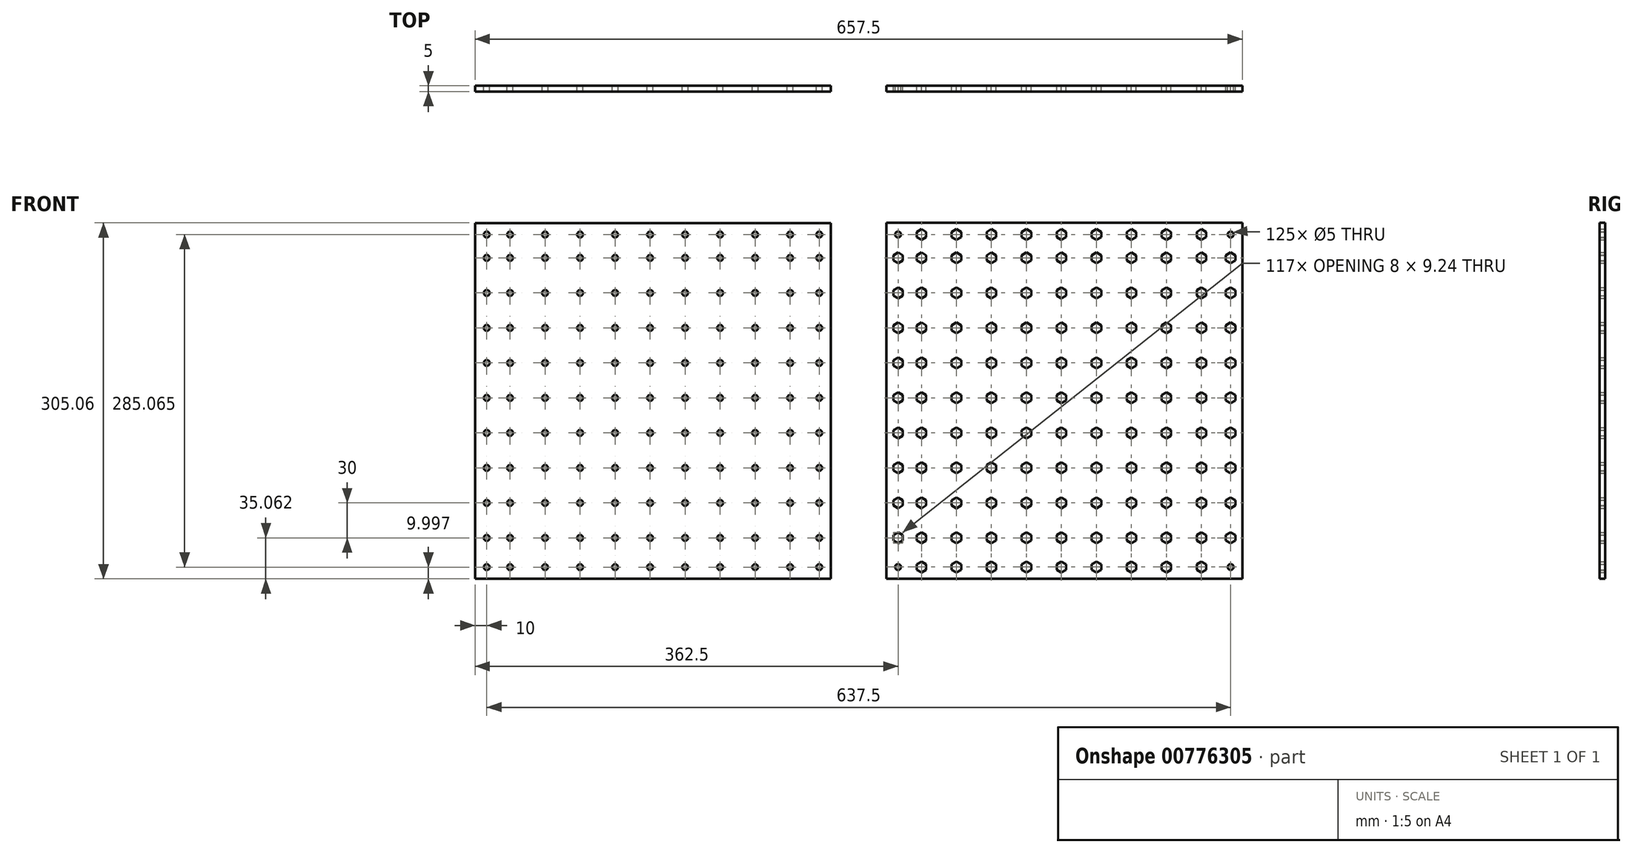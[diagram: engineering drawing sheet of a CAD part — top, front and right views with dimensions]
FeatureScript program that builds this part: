
annotation { "Feature Type Name" : "Feature", "Feature Type Description" : "" }
export const myFeature = defineFeature(function(context is Context, id is Id, definition is map)
    precondition{}
    {
        {
            var Q0;
            Q0=qCreatedBy(makeId("Front.planeOp"),FACE);
            var sketch = newSketch(context, id + "F0", { "sketchPlane" : qUnion([Q0])});
            skLineSegment(sketch, "E0.bottom", {"start": v(-152.5, 134.23) * mm, "end": v(152.5, 134.23) * mm});
            skLineSegment(sketch, "E0.top", {"start": v(-152.5, -170.77) * mm, "end": v(152.5, -170.77) * mm});
            skLineSegment(sketch, "E0.left", {"start": v(-152.5, 134.23) * mm, "end": v(-152.5, -170.77) * mm});
            skLineSegment(sketch, "E0.right", {"start": v(152.5, 134.23) * mm, "end": v(152.5, -170.77) * mm});
            skCircle(sketch, "E1", {"center": v(-142.5, 124.23) * mm, "radius": 2.5 * mm});
            skLineSegment(sketch, "E2", {"start": v(0, 134.23) * mm, "end": v(0, -170.77) * mm, "construction": true});
            skLineSegment(sketch, "E3", {"start": v(-152.5, -18.27) * mm, "end": v(152.5, -18.27) * mm, "construction": true});
            skLineSegment(sketch, "E4.MirrorCS", {"start": v(152.5, -18.27) * mm, "end": v(-152.5, -18.27) * mm, "construction": true});
            skCircle(sketch, "E5.MirrorC", {"center": v(142.5, 124.23) * mm, "radius": 2.5 * mm});
            skCircle(sketch, "E6.MirrorC", {"center": v(-142.5, -160.77) * mm, "radius": 2.5 * mm});
            skCircle(sketch, "E7.MirrorC", {"center": v(142.5, -160.77) * mm, "radius": 2.5 * mm});
            skCircle(sketch, "E8.cCircle", {"center": v(-122.5, 104.23) * mm, "radius": 4 * mm, "construction": true});
            skLineSegment(sketch, "E8.0", {"start": v(-126.5, 106.54) * mm, "end": v(-122.5, 108.85) * mm});
            skLineSegment(sketch, "E8.1", {"start": v(-122.5, 108.85) * mm, "end": v(-118.5, 106.54) * mm});
            skLineSegment(sketch, "E8.2", {"start": v(-118.5, 106.54) * mm, "end": v(-118.5, 101.92) * mm});
            skLineSegment(sketch, "E8.3", {"start": v(-118.5, 101.92) * mm, "end": v(-122.5, 99.61) * mm});
            skLineSegment(sketch, "E8.4", {"start": v(-122.5, 99.61) * mm, "end": v(-126.5, 101.92) * mm});
            skLineSegment(sketch, "E8.5", {"start": v(-126.5, 101.92) * mm, "end": v(-126.5, 106.54) * mm});
            skPoint(sketch, "E8.0.midPoint", {"position": v(-124.5, 107.7) * mm});
            skLineSegment(sketch, "E9.0.1.0", {"start": v(-122.5, 78.85) * mm, "end": v(-118.5, 76.54) * mm});
            skPoint(sketch, "E9.0.1.1", {"position": v(-124.5, 77.7) * mm});
            skLineSegment(sketch, "E9.0.1.2", {"start": v(-122.5, 69.61) * mm, "end": v(-126.5, 71.92) * mm});
            skLineSegment(sketch, "E9.0.1.3", {"start": v(-118.5, 71.92) * mm, "end": v(-122.5, 69.61) * mm});
            skLineSegment(sketch, "E9.0.1.4", {"start": v(-118.5, 76.54) * mm, "end": v(-118.5, 71.92) * mm});
            skLineSegment(sketch, "E9.0.1.5", {"start": v(-126.5, 71.92) * mm, "end": v(-126.5, 76.54) * mm});
            skLineSegment(sketch, "E9.0.1.6", {"start": v(-126.5, 76.54) * mm, "end": v(-122.5, 78.85) * mm});
            skCircle(sketch, "E9.0.1.7", {"center": v(-122.5, 74.23) * mm, "radius": 4 * mm, "construction": true});
            skLineSegment(sketch, "E9.0.2.0", {"start": v(-122.5, 48.85) * mm, "end": v(-118.5, 46.54) * mm});
            skPoint(sketch, "E9.0.2.1", {"position": v(-124.5, 47.7) * mm});
            skLineSegment(sketch, "E9.0.2.2", {"start": v(-122.5, 39.61) * mm, "end": v(-126.5, 41.92) * mm});
            skLineSegment(sketch, "E9.0.2.3", {"start": v(-118.5, 41.92) * mm, "end": v(-122.5, 39.61) * mm});
            skLineSegment(sketch, "E9.0.2.4", {"start": v(-118.5, 46.54) * mm, "end": v(-118.5, 41.92) * mm});
            skLineSegment(sketch, "E9.0.2.5", {"start": v(-126.5, 41.92) * mm, "end": v(-126.5, 46.54) * mm});
            skLineSegment(sketch, "E9.0.2.6", {"start": v(-126.5, 46.54) * mm, "end": v(-122.5, 48.85) * mm});
            skCircle(sketch, "E9.0.2.7", {"center": v(-122.5, 44.23) * mm, "radius": 4 * mm, "construction": true});
            skLineSegment(sketch, "E9.0.3.0", {"start": v(-122.5, 18.85) * mm, "end": v(-118.5, 16.54) * mm});
            skPoint(sketch, "E9.0.3.1", {"position": v(-124.5, 17.7) * mm});
            skLineSegment(sketch, "E9.0.3.2", {"start": v(-122.5, 9.61) * mm, "end": v(-126.5, 11.92) * mm});
            skLineSegment(sketch, "E9.0.3.3", {"start": v(-118.5, 11.92) * mm, "end": v(-122.5, 9.61) * mm});
            skLineSegment(sketch, "E9.0.3.4", {"start": v(-118.5, 16.54) * mm, "end": v(-118.5, 11.92) * mm});
            skLineSegment(sketch, "E9.0.3.5", {"start": v(-126.5, 11.92) * mm, "end": v(-126.5, 16.54) * mm});
            skLineSegment(sketch, "E9.0.3.6", {"start": v(-126.5, 16.54) * mm, "end": v(-122.5, 18.85) * mm});
            skCircle(sketch, "E9.0.3.7", {"center": v(-122.5, 14.23) * mm, "radius": 4 * mm, "construction": true});
            skLineSegment(sketch, "E9.0.4.0", {"start": v(-122.5, -11.15) * mm, "end": v(-118.5, -13.46) * mm});
            skPoint(sketch, "E9.0.4.1", {"position": v(-124.5, -12.3) * mm});
            skLineSegment(sketch, "E9.0.4.2", {"start": v(-122.5, -20.39) * mm, "end": v(-126.5, -18.08) * mm});
            skLineSegment(sketch, "E9.0.4.3", {"start": v(-118.5, -18.08) * mm, "end": v(-122.5, -20.39) * mm});
            skLineSegment(sketch, "E9.0.4.4", {"start": v(-118.5, -13.46) * mm, "end": v(-118.5, -18.08) * mm});
            skLineSegment(sketch, "E9.0.4.5", {"start": v(-126.5, -18.08) * mm, "end": v(-126.5, -13.46) * mm});
            skLineSegment(sketch, "E9.0.4.6", {"start": v(-126.5, -13.46) * mm, "end": v(-122.5, -11.15) * mm});
            skCircle(sketch, "E9.0.4.7", {"center": v(-122.5, -15.77) * mm, "radius": 4 * mm, "construction": true});
            skLineSegment(sketch, "E9.0.5.0", {"start": v(-122.5, -41.15) * mm, "end": v(-118.5, -43.46) * mm});
            skPoint(sketch, "E9.0.5.1", {"position": v(-124.5, -42.3) * mm});
            skLineSegment(sketch, "E9.0.5.2", {"start": v(-122.5, -50.39) * mm, "end": v(-126.5, -48.08) * mm});
            skLineSegment(sketch, "E9.0.5.3", {"start": v(-118.5, -48.08) * mm, "end": v(-122.5, -50.39) * mm});
            skLineSegment(sketch, "E9.0.5.4", {"start": v(-118.5, -43.46) * mm, "end": v(-118.5, -48.08) * mm});
            skLineSegment(sketch, "E9.0.5.5", {"start": v(-126.5, -48.08) * mm, "end": v(-126.5, -43.46) * mm});
            skLineSegment(sketch, "E9.0.5.6", {"start": v(-126.5, -43.46) * mm, "end": v(-122.5, -41.15) * mm});
            skCircle(sketch, "E9.0.5.7", {"center": v(-122.5, -45.77) * mm, "radius": 4 * mm, "construction": true});
            skLineSegment(sketch, "E9.0.6.0", {"start": v(-122.5, -71.15) * mm, "end": v(-118.5, -73.46) * mm});
            skPoint(sketch, "E9.0.6.1", {"position": v(-124.5, -72.3) * mm});
            skLineSegment(sketch, "E9.0.6.2", {"start": v(-122.5, -80.39) * mm, "end": v(-126.5, -78.08) * mm});
            skLineSegment(sketch, "E9.0.6.3", {"start": v(-118.5, -78.08) * mm, "end": v(-122.5, -80.39) * mm});
            skLineSegment(sketch, "E9.0.6.4", {"start": v(-118.5, -73.46) * mm, "end": v(-118.5, -78.08) * mm});
            skLineSegment(sketch, "E9.0.6.5", {"start": v(-126.5, -78.08) * mm, "end": v(-126.5, -73.46) * mm});
            skLineSegment(sketch, "E9.0.6.6", {"start": v(-126.5, -73.46) * mm, "end": v(-122.5, -71.15) * mm});
            skCircle(sketch, "E9.0.6.7", {"center": v(-122.5, -75.77) * mm, "radius": 4 * mm, "construction": true});
            skLineSegment(sketch, "E9.0.7.0", {"start": v(-122.5, -101.15) * mm, "end": v(-118.5, -103.46) * mm});
            skPoint(sketch, "E9.0.7.1", {"position": v(-124.5, -102.3) * mm});
            skLineSegment(sketch, "E9.0.7.2", {"start": v(-122.5, -110.39) * mm, "end": v(-126.5, -108.08) * mm});
            skLineSegment(sketch, "E9.0.7.3", {"start": v(-118.5, -108.08) * mm, "end": v(-122.5, -110.39) * mm});
            skLineSegment(sketch, "E9.0.7.4", {"start": v(-118.5, -103.46) * mm, "end": v(-118.5, -108.08) * mm});
            skLineSegment(sketch, "E9.0.7.5", {"start": v(-126.5, -108.08) * mm, "end": v(-126.5, -103.46) * mm});
            skLineSegment(sketch, "E9.0.7.6", {"start": v(-126.5, -103.46) * mm, "end": v(-122.5, -101.15) * mm});
            skCircle(sketch, "E9.0.7.7", {"center": v(-122.5, -105.77) * mm, "radius": 4 * mm, "construction": true});
            skLineSegment(sketch, "E9.1.0.0", {"start": v(-92.5, 108.85) * mm, "end": v(-88.5, 106.54) * mm});
            skPoint(sketch, "E9.1.0.1", {"position": v(-94.5, 107.7) * mm});
            skLineSegment(sketch, "E9.1.0.2", {"start": v(-92.5, 99.61) * mm, "end": v(-96.5, 101.92) * mm});
            skLineSegment(sketch, "E9.1.0.3", {"start": v(-88.5, 101.92) * mm, "end": v(-92.5, 99.61) * mm});
            skLineSegment(sketch, "E9.1.0.4", {"start": v(-88.5, 106.54) * mm, "end": v(-88.5, 101.92) * mm});
            skLineSegment(sketch, "E9.1.0.5", {"start": v(-96.5, 101.92) * mm, "end": v(-96.5, 106.54) * mm});
            skLineSegment(sketch, "E9.1.0.6", {"start": v(-96.5, 106.54) * mm, "end": v(-92.5, 108.85) * mm});
            skCircle(sketch, "E9.1.0.7", {"center": v(-92.5, 104.23) * mm, "radius": 4 * mm, "construction": true});
            skLineSegment(sketch, "E9.1.1.0", {"start": v(-92.5, 78.85) * mm, "end": v(-88.5, 76.54) * mm});
            skPoint(sketch, "E9.1.1.1", {"position": v(-94.5, 77.7) * mm});
            skLineSegment(sketch, "E9.1.1.2", {"start": v(-92.5, 69.61) * mm, "end": v(-96.5, 71.92) * mm});
            skLineSegment(sketch, "E9.1.1.3", {"start": v(-88.5, 71.92) * mm, "end": v(-92.5, 69.61) * mm});
            skLineSegment(sketch, "E9.1.1.4", {"start": v(-88.5, 76.54) * mm, "end": v(-88.5, 71.92) * mm});
            skLineSegment(sketch, "E9.1.1.5", {"start": v(-96.5, 71.92) * mm, "end": v(-96.5, 76.54) * mm});
            skLineSegment(sketch, "E9.1.1.6", {"start": v(-96.5, 76.54) * mm, "end": v(-92.5, 78.85) * mm});
            skCircle(sketch, "E9.1.1.7", {"center": v(-92.5, 74.23) * mm, "radius": 4 * mm, "construction": true});
            skLineSegment(sketch, "E9.1.2.0", {"start": v(-92.5, 48.85) * mm, "end": v(-88.5, 46.54) * mm});
            skPoint(sketch, "E9.1.2.1", {"position": v(-94.5, 47.7) * mm});
            skLineSegment(sketch, "E9.1.2.2", {"start": v(-92.5, 39.61) * mm, "end": v(-96.5, 41.92) * mm});
            skLineSegment(sketch, "E9.1.2.3", {"start": v(-88.5, 41.92) * mm, "end": v(-92.5, 39.61) * mm});
            skLineSegment(sketch, "E9.1.2.4", {"start": v(-88.5, 46.54) * mm, "end": v(-88.5, 41.92) * mm});
            skLineSegment(sketch, "E9.1.2.5", {"start": v(-96.5, 41.92) * mm, "end": v(-96.5, 46.54) * mm});
            skLineSegment(sketch, "E9.1.2.6", {"start": v(-96.5, 46.54) * mm, "end": v(-92.5, 48.85) * mm});
            skCircle(sketch, "E9.1.2.7", {"center": v(-92.5, 44.23) * mm, "radius": 4 * mm, "construction": true});
            skLineSegment(sketch, "E9.1.3.0", {"start": v(-92.5, 18.85) * mm, "end": v(-88.5, 16.54) * mm});
            skPoint(sketch, "E9.1.3.1", {"position": v(-94.5, 17.7) * mm});
            skLineSegment(sketch, "E9.1.3.2", {"start": v(-92.5, 9.61) * mm, "end": v(-96.5, 11.92) * mm});
            skLineSegment(sketch, "E9.1.3.3", {"start": v(-88.5, 11.92) * mm, "end": v(-92.5, 9.61) * mm});
            skLineSegment(sketch, "E9.1.3.4", {"start": v(-88.5, 16.54) * mm, "end": v(-88.5, 11.92) * mm});
            skLineSegment(sketch, "E9.1.3.5", {"start": v(-96.5, 11.92) * mm, "end": v(-96.5, 16.54) * mm});
            skLineSegment(sketch, "E9.1.3.6", {"start": v(-96.5, 16.54) * mm, "end": v(-92.5, 18.85) * mm});
            skCircle(sketch, "E9.1.3.7", {"center": v(-92.5, 14.23) * mm, "radius": 4 * mm, "construction": true});
            skLineSegment(sketch, "E9.1.4.0", {"start": v(-92.5, -11.15) * mm, "end": v(-88.5, -13.46) * mm});
            skPoint(sketch, "E9.1.4.1", {"position": v(-94.5, -12.3) * mm});
            skLineSegment(sketch, "E9.1.4.2", {"start": v(-92.5, -20.39) * mm, "end": v(-96.5, -18.08) * mm});
            skLineSegment(sketch, "E9.1.4.3", {"start": v(-88.5, -18.08) * mm, "end": v(-92.5, -20.39) * mm});
            skLineSegment(sketch, "E9.1.4.4", {"start": v(-88.5, -13.46) * mm, "end": v(-88.5, -18.08) * mm});
            skLineSegment(sketch, "E9.1.4.5", {"start": v(-96.5, -18.08) * mm, "end": v(-96.5, -13.46) * mm});
            skLineSegment(sketch, "E9.1.4.6", {"start": v(-96.5, -13.46) * mm, "end": v(-92.5, -11.15) * mm});
            skCircle(sketch, "E9.1.4.7", {"center": v(-92.5, -15.77) * mm, "radius": 4 * mm, "construction": true});
            skLineSegment(sketch, "E9.1.5.0", {"start": v(-92.5, -41.15) * mm, "end": v(-88.5, -43.46) * mm});
            skPoint(sketch, "E9.1.5.1", {"position": v(-94.5, -42.3) * mm});
            skLineSegment(sketch, "E9.1.5.2", {"start": v(-92.5, -50.39) * mm, "end": v(-96.5, -48.08) * mm});
            skLineSegment(sketch, "E9.1.5.3", {"start": v(-88.5, -48.08) * mm, "end": v(-92.5, -50.39) * mm});
            skLineSegment(sketch, "E9.1.5.4", {"start": v(-88.5, -43.46) * mm, "end": v(-88.5, -48.08) * mm});
            skLineSegment(sketch, "E9.1.5.5", {"start": v(-96.5, -48.08) * mm, "end": v(-96.5, -43.46) * mm});
            skLineSegment(sketch, "E9.1.5.6", {"start": v(-96.5, -43.46) * mm, "end": v(-92.5, -41.15) * mm});
            skCircle(sketch, "E9.1.5.7", {"center": v(-92.5, -45.77) * mm, "radius": 4 * mm, "construction": true});
            skLineSegment(sketch, "E9.1.6.0", {"start": v(-92.5, -71.15) * mm, "end": v(-88.5, -73.46) * mm});
            skPoint(sketch, "E9.1.6.1", {"position": v(-94.5, -72.3) * mm});
            skLineSegment(sketch, "E9.1.6.2", {"start": v(-92.5, -80.39) * mm, "end": v(-96.5, -78.08) * mm});
            skLineSegment(sketch, "E9.1.6.3", {"start": v(-88.5, -78.08) * mm, "end": v(-92.5, -80.39) * mm});
            skLineSegment(sketch, "E9.1.6.4", {"start": v(-88.5, -73.46) * mm, "end": v(-88.5, -78.08) * mm});
            skLineSegment(sketch, "E9.1.6.5", {"start": v(-96.5, -78.08) * mm, "end": v(-96.5, -73.46) * mm});
            skLineSegment(sketch, "E9.1.6.6", {"start": v(-96.5, -73.46) * mm, "end": v(-92.5, -71.15) * mm});
            skCircle(sketch, "E9.1.6.7", {"center": v(-92.5, -75.77) * mm, "radius": 4 * mm, "construction": true});
            skLineSegment(sketch, "E9.1.7.0", {"start": v(-92.5, -101.15) * mm, "end": v(-88.5, -103.46) * mm});
            skPoint(sketch, "E9.1.7.1", {"position": v(-94.5, -102.3) * mm});
            skLineSegment(sketch, "E9.1.7.2", {"start": v(-92.5, -110.39) * mm, "end": v(-96.5, -108.08) * mm});
            skLineSegment(sketch, "E9.1.7.3", {"start": v(-88.5, -108.08) * mm, "end": v(-92.5, -110.39) * mm});
            skLineSegment(sketch, "E9.1.7.4", {"start": v(-88.5, -103.46) * mm, "end": v(-88.5, -108.08) * mm});
            skLineSegment(sketch, "E9.1.7.5", {"start": v(-96.5, -108.08) * mm, "end": v(-96.5, -103.46) * mm});
            skLineSegment(sketch, "E9.1.7.6", {"start": v(-96.5, -103.46) * mm, "end": v(-92.5, -101.15) * mm});
            skCircle(sketch, "E9.1.7.7", {"center": v(-92.5, -105.77) * mm, "radius": 4 * mm, "construction": true});
            skLineSegment(sketch, "E9.2.0.0", {"start": v(-62.5, 108.85) * mm, "end": v(-58.5, 106.54) * mm});
            skPoint(sketch, "E9.2.0.1", {"position": v(-64.5, 107.7) * mm});
            skLineSegment(sketch, "E9.2.0.2", {"start": v(-62.5, 99.61) * mm, "end": v(-66.5, 101.92) * mm});
            skLineSegment(sketch, "E9.2.0.3", {"start": v(-58.5, 101.92) * mm, "end": v(-62.5, 99.61) * mm});
            skLineSegment(sketch, "E9.2.0.4", {"start": v(-58.5, 106.54) * mm, "end": v(-58.5, 101.92) * mm});
            skLineSegment(sketch, "E9.2.0.5", {"start": v(-66.5, 101.92) * mm, "end": v(-66.5, 106.54) * mm});
            skLineSegment(sketch, "E9.2.0.6", {"start": v(-66.5, 106.54) * mm, "end": v(-62.5, 108.85) * mm});
            skCircle(sketch, "E9.2.0.7", {"center": v(-62.5, 104.23) * mm, "radius": 4 * mm, "construction": true});
            skLineSegment(sketch, "E9.2.1.0", {"start": v(-62.5, 78.85) * mm, "end": v(-58.5, 76.54) * mm});
            skPoint(sketch, "E9.2.1.1", {"position": v(-64.5, 77.7) * mm});
            skLineSegment(sketch, "E9.2.1.2", {"start": v(-62.5, 69.61) * mm, "end": v(-66.5, 71.92) * mm});
            skLineSegment(sketch, "E9.2.1.3", {"start": v(-58.5, 71.92) * mm, "end": v(-62.5, 69.61) * mm});
            skLineSegment(sketch, "E9.2.1.4", {"start": v(-58.5, 76.54) * mm, "end": v(-58.5, 71.92) * mm});
            skLineSegment(sketch, "E9.2.1.5", {"start": v(-66.5, 71.92) * mm, "end": v(-66.5, 76.54) * mm});
            skLineSegment(sketch, "E9.2.1.6", {"start": v(-66.5, 76.54) * mm, "end": v(-62.5, 78.85) * mm});
            skCircle(sketch, "E9.2.1.7", {"center": v(-62.5, 74.23) * mm, "radius": 4 * mm, "construction": true});
            skLineSegment(sketch, "E9.2.2.0", {"start": v(-62.5, 48.85) * mm, "end": v(-58.5, 46.54) * mm});
            skPoint(sketch, "E9.2.2.1", {"position": v(-64.5, 47.7) * mm});
            skLineSegment(sketch, "E9.2.2.2", {"start": v(-62.5, 39.61) * mm, "end": v(-66.5, 41.92) * mm});
            skLineSegment(sketch, "E9.2.2.3", {"start": v(-58.5, 41.92) * mm, "end": v(-62.5, 39.61) * mm});
            skLineSegment(sketch, "E9.2.2.4", {"start": v(-58.5, 46.54) * mm, "end": v(-58.5, 41.92) * mm});
            skLineSegment(sketch, "E9.2.2.5", {"start": v(-66.5, 41.92) * mm, "end": v(-66.5, 46.54) * mm});
            skLineSegment(sketch, "E9.2.2.6", {"start": v(-66.5, 46.54) * mm, "end": v(-62.5, 48.85) * mm});
            skCircle(sketch, "E9.2.2.7", {"center": v(-62.5, 44.23) * mm, "radius": 4 * mm, "construction": true});
            skLineSegment(sketch, "E9.2.3.0", {"start": v(-62.5, 18.85) * mm, "end": v(-58.5, 16.54) * mm});
            skPoint(sketch, "E9.2.3.1", {"position": v(-64.5, 17.7) * mm});
            skLineSegment(sketch, "E9.2.3.2", {"start": v(-62.5, 9.61) * mm, "end": v(-66.5, 11.92) * mm});
            skLineSegment(sketch, "E9.2.3.3", {"start": v(-58.5, 11.92) * mm, "end": v(-62.5, 9.61) * mm});
            skLineSegment(sketch, "E9.2.3.4", {"start": v(-58.5, 16.54) * mm, "end": v(-58.5, 11.92) * mm});
            skLineSegment(sketch, "E9.2.3.5", {"start": v(-66.5, 11.92) * mm, "end": v(-66.5, 16.54) * mm});
            skLineSegment(sketch, "E9.2.3.6", {"start": v(-66.5, 16.54) * mm, "end": v(-62.5, 18.85) * mm});
            skCircle(sketch, "E9.2.3.7", {"center": v(-62.5, 14.23) * mm, "radius": 4 * mm, "construction": true});
            skLineSegment(sketch, "E9.2.4.0", {"start": v(-62.5, -11.15) * mm, "end": v(-58.5, -13.46) * mm});
            skPoint(sketch, "E9.2.4.1", {"position": v(-64.5, -12.3) * mm});
            skLineSegment(sketch, "E9.2.4.2", {"start": v(-62.5, -20.39) * mm, "end": v(-66.5, -18.08) * mm});
            skLineSegment(sketch, "E9.2.4.3", {"start": v(-58.5, -18.08) * mm, "end": v(-62.5, -20.39) * mm});
            skLineSegment(sketch, "E9.2.4.4", {"start": v(-58.5, -13.46) * mm, "end": v(-58.5, -18.08) * mm});
            skLineSegment(sketch, "E9.2.4.5", {"start": v(-66.5, -18.08) * mm, "end": v(-66.5, -13.46) * mm});
            skLineSegment(sketch, "E9.2.4.6", {"start": v(-66.5, -13.46) * mm, "end": v(-62.5, -11.15) * mm});
            skCircle(sketch, "E9.2.4.7", {"center": v(-62.5, -15.77) * mm, "radius": 4 * mm, "construction": true});
            skLineSegment(sketch, "E9.2.5.0", {"start": v(-62.5, -41.15) * mm, "end": v(-58.5, -43.46) * mm});
            skPoint(sketch, "E9.2.5.1", {"position": v(-64.5, -42.3) * mm});
            skLineSegment(sketch, "E9.2.5.2", {"start": v(-62.5, -50.39) * mm, "end": v(-66.5, -48.08) * mm});
            skLineSegment(sketch, "E9.2.5.3", {"start": v(-58.5, -48.08) * mm, "end": v(-62.5, -50.39) * mm});
            skLineSegment(sketch, "E9.2.5.4", {"start": v(-58.5, -43.46) * mm, "end": v(-58.5, -48.08) * mm});
            skLineSegment(sketch, "E9.2.5.5", {"start": v(-66.5, -48.08) * mm, "end": v(-66.5, -43.46) * mm});
            skLineSegment(sketch, "E9.2.5.6", {"start": v(-66.5, -43.46) * mm, "end": v(-62.5, -41.15) * mm});
            skCircle(sketch, "E9.2.5.7", {"center": v(-62.5, -45.77) * mm, "radius": 4 * mm, "construction": true});
            skLineSegment(sketch, "E9.2.6.0", {"start": v(-62.5, -71.15) * mm, "end": v(-58.5, -73.46) * mm});
            skPoint(sketch, "E9.2.6.1", {"position": v(-64.5, -72.3) * mm});
            skLineSegment(sketch, "E9.2.6.2", {"start": v(-62.5, -80.39) * mm, "end": v(-66.5, -78.08) * mm});
            skLineSegment(sketch, "E9.2.6.3", {"start": v(-58.5, -78.08) * mm, "end": v(-62.5, -80.39) * mm});
            skLineSegment(sketch, "E9.2.6.4", {"start": v(-58.5, -73.46) * mm, "end": v(-58.5, -78.08) * mm});
            skLineSegment(sketch, "E9.2.6.5", {"start": v(-66.5, -78.08) * mm, "end": v(-66.5, -73.46) * mm});
            skLineSegment(sketch, "E9.2.6.6", {"start": v(-66.5, -73.46) * mm, "end": v(-62.5, -71.15) * mm});
            skCircle(sketch, "E9.2.6.7", {"center": v(-62.5, -75.77) * mm, "radius": 4 * mm, "construction": true});
            skLineSegment(sketch, "E9.2.7.0", {"start": v(-62.5, -101.15) * mm, "end": v(-58.5, -103.46) * mm});
            skPoint(sketch, "E9.2.7.1", {"position": v(-64.5, -102.3) * mm});
            skLineSegment(sketch, "E9.2.7.2", {"start": v(-62.5, -110.39) * mm, "end": v(-66.5, -108.08) * mm});
            skLineSegment(sketch, "E9.2.7.3", {"start": v(-58.5, -108.08) * mm, "end": v(-62.5, -110.39) * mm});
            skLineSegment(sketch, "E9.2.7.4", {"start": v(-58.5, -103.46) * mm, "end": v(-58.5, -108.08) * mm});
            skLineSegment(sketch, "E9.2.7.5", {"start": v(-66.5, -108.08) * mm, "end": v(-66.5, -103.46) * mm});
            skLineSegment(sketch, "E9.2.7.6", {"start": v(-66.5, -103.46) * mm, "end": v(-62.5, -101.15) * mm});
            skCircle(sketch, "E9.2.7.7", {"center": v(-62.5, -105.77) * mm, "radius": 4 * mm, "construction": true});
            skLineSegment(sketch, "E9.3.0.0", {"start": v(-32.5, 108.85) * mm, "end": v(-28.5, 106.54) * mm});
            skPoint(sketch, "E9.3.0.1", {"position": v(-34.5, 107.7) * mm});
            skLineSegment(sketch, "E9.3.0.2", {"start": v(-32.5, 99.61) * mm, "end": v(-36.5, 101.92) * mm});
            skLineSegment(sketch, "E9.3.0.3", {"start": v(-28.5, 101.92) * mm, "end": v(-32.5, 99.61) * mm});
            skLineSegment(sketch, "E9.3.0.4", {"start": v(-28.5, 106.54) * mm, "end": v(-28.5, 101.92) * mm});
            skLineSegment(sketch, "E9.3.0.5", {"start": v(-36.5, 101.92) * mm, "end": v(-36.5, 106.54) * mm});
            skLineSegment(sketch, "E9.3.0.6", {"start": v(-36.5, 106.54) * mm, "end": v(-32.5, 108.85) * mm});
            skCircle(sketch, "E9.3.0.7", {"center": v(-32.5, 104.23) * mm, "radius": 4 * mm, "construction": true});
            skLineSegment(sketch, "E9.3.1.0", {"start": v(-32.5, 78.85) * mm, "end": v(-28.5, 76.54) * mm});
            skPoint(sketch, "E9.3.1.1", {"position": v(-34.5, 77.7) * mm});
            skLineSegment(sketch, "E9.3.1.2", {"start": v(-32.5, 69.61) * mm, "end": v(-36.5, 71.92) * mm});
            skLineSegment(sketch, "E9.3.1.3", {"start": v(-28.5, 71.92) * mm, "end": v(-32.5, 69.61) * mm});
            skLineSegment(sketch, "E9.3.1.4", {"start": v(-28.5, 76.54) * mm, "end": v(-28.5, 71.92) * mm});
            skLineSegment(sketch, "E9.3.1.5", {"start": v(-36.5, 71.92) * mm, "end": v(-36.5, 76.54) * mm});
            skLineSegment(sketch, "E9.3.1.6", {"start": v(-36.5, 76.54) * mm, "end": v(-32.5, 78.85) * mm});
            skCircle(sketch, "E9.3.1.7", {"center": v(-32.5, 74.23) * mm, "radius": 4 * mm, "construction": true});
            skLineSegment(sketch, "E9.3.2.0", {"start": v(-32.5, 48.85) * mm, "end": v(-28.5, 46.54) * mm});
            skPoint(sketch, "E9.3.2.1", {"position": v(-34.5, 47.7) * mm});
            skLineSegment(sketch, "E9.3.2.2", {"start": v(-32.5, 39.61) * mm, "end": v(-36.5, 41.92) * mm});
            skLineSegment(sketch, "E9.3.2.3", {"start": v(-28.5, 41.92) * mm, "end": v(-32.5, 39.61) * mm});
            skLineSegment(sketch, "E9.3.2.4", {"start": v(-28.5, 46.54) * mm, "end": v(-28.5, 41.92) * mm});
            skLineSegment(sketch, "E9.3.2.5", {"start": v(-36.5, 41.92) * mm, "end": v(-36.5, 46.54) * mm});
            skLineSegment(sketch, "E9.3.2.6", {"start": v(-36.5, 46.54) * mm, "end": v(-32.5, 48.85) * mm});
            skCircle(sketch, "E9.3.2.7", {"center": v(-32.5, 44.23) * mm, "radius": 4 * mm, "construction": true});
            skLineSegment(sketch, "E9.3.3.0", {"start": v(-32.5, 18.85) * mm, "end": v(-28.5, 16.54) * mm});
            skPoint(sketch, "E9.3.3.1", {"position": v(-34.5, 17.7) * mm});
            skLineSegment(sketch, "E9.3.3.2", {"start": v(-32.5, 9.61) * mm, "end": v(-36.5, 11.92) * mm});
            skLineSegment(sketch, "E9.3.3.3", {"start": v(-28.5, 11.92) * mm, "end": v(-32.5, 9.61) * mm});
            skLineSegment(sketch, "E9.3.3.4", {"start": v(-28.5, 16.54) * mm, "end": v(-28.5, 11.92) * mm});
            skLineSegment(sketch, "E9.3.3.5", {"start": v(-36.5, 11.92) * mm, "end": v(-36.5, 16.54) * mm});
            skLineSegment(sketch, "E9.3.3.6", {"start": v(-36.5, 16.54) * mm, "end": v(-32.5, 18.85) * mm});
            skCircle(sketch, "E9.3.3.7", {"center": v(-32.5, 14.23) * mm, "radius": 4 * mm, "construction": true});
            skLineSegment(sketch, "E9.3.4.0", {"start": v(-32.5, -11.15) * mm, "end": v(-28.5, -13.46) * mm});
            skPoint(sketch, "E9.3.4.1", {"position": v(-34.5, -12.3) * mm});
            skLineSegment(sketch, "E9.3.4.2", {"start": v(-32.5, -20.39) * mm, "end": v(-36.5, -18.08) * mm});
            skLineSegment(sketch, "E9.3.4.3", {"start": v(-28.5, -18.08) * mm, "end": v(-32.5, -20.39) * mm});
            skLineSegment(sketch, "E9.3.4.4", {"start": v(-28.5, -13.46) * mm, "end": v(-28.5, -18.08) * mm});
            skLineSegment(sketch, "E9.3.4.5", {"start": v(-36.5, -18.08) * mm, "end": v(-36.5, -13.46) * mm});
            skLineSegment(sketch, "E9.3.4.6", {"start": v(-36.5, -13.46) * mm, "end": v(-32.5, -11.15) * mm});
            skCircle(sketch, "E9.3.4.7", {"center": v(-32.5, -15.77) * mm, "radius": 4 * mm, "construction": true});
            skLineSegment(sketch, "E9.3.5.0", {"start": v(-32.5, -41.15) * mm, "end": v(-28.5, -43.46) * mm});
            skPoint(sketch, "E9.3.5.1", {"position": v(-34.5, -42.3) * mm});
            skLineSegment(sketch, "E9.3.5.2", {"start": v(-32.5, -50.39) * mm, "end": v(-36.5, -48.08) * mm});
            skLineSegment(sketch, "E9.3.5.3", {"start": v(-28.5, -48.08) * mm, "end": v(-32.5, -50.39) * mm});
            skLineSegment(sketch, "E9.3.5.4", {"start": v(-28.5, -43.46) * mm, "end": v(-28.5, -48.08) * mm});
            skLineSegment(sketch, "E9.3.5.5", {"start": v(-36.5, -48.08) * mm, "end": v(-36.5, -43.46) * mm});
            skLineSegment(sketch, "E9.3.5.6", {"start": v(-36.5, -43.46) * mm, "end": v(-32.5, -41.15) * mm});
            skCircle(sketch, "E9.3.5.7", {"center": v(-32.5, -45.77) * mm, "radius": 4 * mm, "construction": true});
            skLineSegment(sketch, "E9.3.6.0", {"start": v(-32.5, -71.15) * mm, "end": v(-28.5, -73.46) * mm});
            skPoint(sketch, "E9.3.6.1", {"position": v(-34.5, -72.3) * mm});
            skLineSegment(sketch, "E9.3.6.2", {"start": v(-32.5, -80.39) * mm, "end": v(-36.5, -78.08) * mm});
            skLineSegment(sketch, "E9.3.6.3", {"start": v(-28.5, -78.08) * mm, "end": v(-32.5, -80.39) * mm});
            skLineSegment(sketch, "E9.3.6.4", {"start": v(-28.5, -73.46) * mm, "end": v(-28.5, -78.08) * mm});
            skLineSegment(sketch, "E9.3.6.5", {"start": v(-36.5, -78.08) * mm, "end": v(-36.5, -73.46) * mm});
            skLineSegment(sketch, "E9.3.6.6", {"start": v(-36.5, -73.46) * mm, "end": v(-32.5, -71.15) * mm});
            skCircle(sketch, "E9.3.6.7", {"center": v(-32.5, -75.77) * mm, "radius": 4 * mm, "construction": true});
            skLineSegment(sketch, "E9.3.7.0", {"start": v(-32.5, -101.15) * mm, "end": v(-28.5, -103.46) * mm});
            skPoint(sketch, "E9.3.7.1", {"position": v(-34.5, -102.3) * mm});
            skLineSegment(sketch, "E9.3.7.2", {"start": v(-32.5, -110.39) * mm, "end": v(-36.5, -108.08) * mm});
            skLineSegment(sketch, "E9.3.7.3", {"start": v(-28.5, -108.08) * mm, "end": v(-32.5, -110.39) * mm});
            skLineSegment(sketch, "E9.3.7.4", {"start": v(-28.5, -103.46) * mm, "end": v(-28.5, -108.08) * mm});
            skLineSegment(sketch, "E9.3.7.5", {"start": v(-36.5, -108.08) * mm, "end": v(-36.5, -103.46) * mm});
            skLineSegment(sketch, "E9.3.7.6", {"start": v(-36.5, -103.46) * mm, "end": v(-32.5, -101.15) * mm});
            skCircle(sketch, "E9.3.7.7", {"center": v(-32.5, -105.77) * mm, "radius": 4 * mm, "construction": true});
            skLineSegment(sketch, "E9.4.0.0", {"start": v(-2.5, 108.85) * mm, "end": v(1.5, 106.54) * mm});
            skPoint(sketch, "E9.4.0.1", {"position": v(-4.5, 107.7) * mm});
            skLineSegment(sketch, "E9.4.0.2", {"start": v(-2.5, 99.61) * mm, "end": v(-6.5, 101.92) * mm});
            skLineSegment(sketch, "E9.4.0.3", {"start": v(1.5, 101.92) * mm, "end": v(-2.5, 99.61) * mm});
            skLineSegment(sketch, "E9.4.0.4", {"start": v(1.5, 106.54) * mm, "end": v(1.5, 101.92) * mm});
            skLineSegment(sketch, "E9.4.0.5", {"start": v(-6.5, 101.92) * mm, "end": v(-6.5, 106.54) * mm});
            skLineSegment(sketch, "E9.4.0.6", {"start": v(-6.5, 106.54) * mm, "end": v(-2.5, 108.85) * mm});
            skCircle(sketch, "E9.4.0.7", {"center": v(-2.5, 104.23) * mm, "radius": 4 * mm, "construction": true});
            skLineSegment(sketch, "E9.4.1.0", {"start": v(-2.5, 78.85) * mm, "end": v(1.5, 76.54) * mm});
            skPoint(sketch, "E9.4.1.1", {"position": v(-4.5, 77.7) * mm});
            skLineSegment(sketch, "E9.4.1.2", {"start": v(-2.5, 69.61) * mm, "end": v(-6.5, 71.92) * mm});
            skLineSegment(sketch, "E9.4.1.3", {"start": v(1.5, 71.92) * mm, "end": v(-2.5, 69.61) * mm});
            skLineSegment(sketch, "E9.4.1.4", {"start": v(1.5, 76.54) * mm, "end": v(1.5, 71.92) * mm});
            skLineSegment(sketch, "E9.4.1.5", {"start": v(-6.5, 71.92) * mm, "end": v(-6.5, 76.54) * mm});
            skLineSegment(sketch, "E9.4.1.6", {"start": v(-6.5, 76.54) * mm, "end": v(-2.5, 78.85) * mm});
            skCircle(sketch, "E9.4.1.7", {"center": v(-2.5, 74.23) * mm, "radius": 4 * mm, "construction": true});
            skLineSegment(sketch, "E9.4.2.0", {"start": v(-2.5, 48.85) * mm, "end": v(1.5, 46.54) * mm});
            skPoint(sketch, "E9.4.2.1", {"position": v(-4.5, 47.7) * mm});
            skLineSegment(sketch, "E9.4.2.2", {"start": v(-2.5, 39.61) * mm, "end": v(-6.5, 41.92) * mm});
            skLineSegment(sketch, "E9.4.2.3", {"start": v(1.5, 41.92) * mm, "end": v(-2.5, 39.61) * mm});
            skLineSegment(sketch, "E9.4.2.4", {"start": v(1.5, 46.54) * mm, "end": v(1.5, 41.92) * mm});
            skLineSegment(sketch, "E9.4.2.5", {"start": v(-6.5, 41.92) * mm, "end": v(-6.5, 46.54) * mm});
            skLineSegment(sketch, "E9.4.2.6", {"start": v(-6.5, 46.54) * mm, "end": v(-2.5, 48.85) * mm});
            skCircle(sketch, "E9.4.2.7", {"center": v(-2.5, 44.23) * mm, "radius": 4 * mm, "construction": true});
            skLineSegment(sketch, "E9.4.3.0", {"start": v(-2.5, 18.85) * mm, "end": v(1.5, 16.54) * mm});
            skPoint(sketch, "E9.4.3.1", {"position": v(-4.5, 17.7) * mm});
            skLineSegment(sketch, "E9.4.3.2", {"start": v(-2.5, 9.61) * mm, "end": v(-6.5, 11.92) * mm});
            skLineSegment(sketch, "E9.4.3.3", {"start": v(1.5, 11.92) * mm, "end": v(-2.5, 9.61) * mm});
            skLineSegment(sketch, "E9.4.3.4", {"start": v(1.5, 16.54) * mm, "end": v(1.5, 11.92) * mm});
            skLineSegment(sketch, "E9.4.3.5", {"start": v(-6.5, 11.92) * mm, "end": v(-6.5, 16.54) * mm});
            skLineSegment(sketch, "E9.4.3.6", {"start": v(-6.5, 16.54) * mm, "end": v(-2.5, 18.85) * mm});
            skCircle(sketch, "E9.4.3.7", {"center": v(-2.5, 14.23) * mm, "radius": 4 * mm, "construction": true});
            skLineSegment(sketch, "E9.4.4.0", {"start": v(-2.5, -11.15) * mm, "end": v(1.5, -13.46) * mm});
            skPoint(sketch, "E9.4.4.1", {"position": v(-4.5, -12.3) * mm});
            skLineSegment(sketch, "E9.4.4.2", {"start": v(-2.5, -20.39) * mm, "end": v(-6.5, -18.08) * mm});
            skLineSegment(sketch, "E9.4.4.3", {"start": v(1.5, -18.08) * mm, "end": v(-2.5, -20.39) * mm});
            skLineSegment(sketch, "E9.4.4.4", {"start": v(1.5, -13.46) * mm, "end": v(1.5, -18.08) * mm});
            skLineSegment(sketch, "E9.4.4.5", {"start": v(-6.5, -18.08) * mm, "end": v(-6.5, -13.46) * mm});
            skLineSegment(sketch, "E9.4.4.6", {"start": v(-6.5, -13.46) * mm, "end": v(-2.5, -11.15) * mm});
            skCircle(sketch, "E9.4.4.7", {"center": v(-2.5, -15.77) * mm, "radius": 4 * mm, "construction": true});
            skLineSegment(sketch, "E9.4.5.0", {"start": v(-2.5, -41.15) * mm, "end": v(1.5, -43.46) * mm});
            skPoint(sketch, "E9.4.5.1", {"position": v(-4.5, -42.3) * mm});
            skLineSegment(sketch, "E9.4.5.2", {"start": v(-2.5, -50.39) * mm, "end": v(-6.5, -48.08) * mm});
            skLineSegment(sketch, "E9.4.5.3", {"start": v(1.5, -48.08) * mm, "end": v(-2.5, -50.39) * mm});
            skLineSegment(sketch, "E9.4.5.4", {"start": v(1.5, -43.46) * mm, "end": v(1.5, -48.08) * mm});
            skLineSegment(sketch, "E9.4.5.5", {"start": v(-6.5, -48.08) * mm, "end": v(-6.5, -43.46) * mm});
            skLineSegment(sketch, "E9.4.5.6", {"start": v(-6.5, -43.46) * mm, "end": v(-2.5, -41.15) * mm});
            skCircle(sketch, "E9.4.5.7", {"center": v(-2.5, -45.77) * mm, "radius": 4 * mm, "construction": true});
            skLineSegment(sketch, "E9.4.6.0", {"start": v(-2.5, -71.15) * mm, "end": v(1.5, -73.46) * mm});
            skPoint(sketch, "E9.4.6.1", {"position": v(-4.5, -72.3) * mm});
            skLineSegment(sketch, "E9.4.6.2", {"start": v(-2.5, -80.39) * mm, "end": v(-6.5, -78.08) * mm});
            skLineSegment(sketch, "E9.4.6.3", {"start": v(1.5, -78.08) * mm, "end": v(-2.5, -80.39) * mm});
            skLineSegment(sketch, "E9.4.6.4", {"start": v(1.5, -73.46) * mm, "end": v(1.5, -78.08) * mm});
            skLineSegment(sketch, "E9.4.6.5", {"start": v(-6.5, -78.08) * mm, "end": v(-6.5, -73.46) * mm});
            skLineSegment(sketch, "E9.4.6.6", {"start": v(-6.5, -73.46) * mm, "end": v(-2.5, -71.15) * mm});
            skCircle(sketch, "E9.4.6.7", {"center": v(-2.5, -75.77) * mm, "radius": 4 * mm, "construction": true});
            skLineSegment(sketch, "E9.4.7.0", {"start": v(-2.5, -101.15) * mm, "end": v(1.5, -103.46) * mm});
            skPoint(sketch, "E9.4.7.1", {"position": v(-4.5, -102.3) * mm});
            skLineSegment(sketch, "E9.4.7.2", {"start": v(-2.5, -110.39) * mm, "end": v(-6.5, -108.08) * mm});
            skLineSegment(sketch, "E9.4.7.3", {"start": v(1.5, -108.08) * mm, "end": v(-2.5, -110.39) * mm});
            skLineSegment(sketch, "E9.4.7.4", {"start": v(1.5, -103.46) * mm, "end": v(1.5, -108.08) * mm});
            skLineSegment(sketch, "E9.4.7.5", {"start": v(-6.5, -108.08) * mm, "end": v(-6.5, -103.46) * mm});
            skLineSegment(sketch, "E9.4.7.6", {"start": v(-6.5, -103.46) * mm, "end": v(-2.5, -101.15) * mm});
            skCircle(sketch, "E9.4.7.7", {"center": v(-2.5, -105.77) * mm, "radius": 4 * mm, "construction": true});
            skLineSegment(sketch, "E9.5.0.0", {"start": v(27.5, 108.85) * mm, "end": v(31.5, 106.54) * mm});
            skPoint(sketch, "E9.5.0.1", {"position": v(25.5, 107.7) * mm});
            skLineSegment(sketch, "E9.5.0.2", {"start": v(27.5, 99.61) * mm, "end": v(23.5, 101.92) * mm});
            skLineSegment(sketch, "E9.5.0.3", {"start": v(31.5, 101.92) * mm, "end": v(27.5, 99.61) * mm});
            skLineSegment(sketch, "E9.5.0.4", {"start": v(31.5, 106.54) * mm, "end": v(31.5, 101.92) * mm});
            skLineSegment(sketch, "E9.5.0.5", {"start": v(23.5, 101.92) * mm, "end": v(23.5, 106.54) * mm});
            skLineSegment(sketch, "E9.5.0.6", {"start": v(23.5, 106.54) * mm, "end": v(27.5, 108.85) * mm});
            skCircle(sketch, "E9.5.0.7", {"center": v(27.5, 104.23) * mm, "radius": 4 * mm, "construction": true});
            skLineSegment(sketch, "E9.5.1.0", {"start": v(27.5, 78.85) * mm, "end": v(31.5, 76.54) * mm});
            skPoint(sketch, "E9.5.1.1", {"position": v(25.5, 77.7) * mm});
            skLineSegment(sketch, "E9.5.1.2", {"start": v(27.5, 69.61) * mm, "end": v(23.5, 71.92) * mm});
            skLineSegment(sketch, "E9.5.1.3", {"start": v(31.5, 71.92) * mm, "end": v(27.5, 69.61) * mm});
            skLineSegment(sketch, "E9.5.1.4", {"start": v(31.5, 76.54) * mm, "end": v(31.5, 71.92) * mm});
            skLineSegment(sketch, "E9.5.1.5", {"start": v(23.5, 71.92) * mm, "end": v(23.5, 76.54) * mm});
            skLineSegment(sketch, "E9.5.1.6", {"start": v(23.5, 76.54) * mm, "end": v(27.5, 78.85) * mm});
            skCircle(sketch, "E9.5.1.7", {"center": v(27.5, 74.23) * mm, "radius": 4 * mm, "construction": true});
            skLineSegment(sketch, "E9.5.2.0", {"start": v(27.5, 48.85) * mm, "end": v(31.5, 46.54) * mm});
            skPoint(sketch, "E9.5.2.1", {"position": v(25.5, 47.7) * mm});
            skLineSegment(sketch, "E9.5.2.2", {"start": v(27.5, 39.61) * mm, "end": v(23.5, 41.92) * mm});
            skLineSegment(sketch, "E9.5.2.3", {"start": v(31.5, 41.92) * mm, "end": v(27.5, 39.61) * mm});
            skLineSegment(sketch, "E9.5.2.4", {"start": v(31.5, 46.54) * mm, "end": v(31.5, 41.92) * mm});
            skLineSegment(sketch, "E9.5.2.5", {"start": v(23.5, 41.92) * mm, "end": v(23.5, 46.54) * mm});
            skLineSegment(sketch, "E9.5.2.6", {"start": v(23.5, 46.54) * mm, "end": v(27.5, 48.85) * mm});
            skCircle(sketch, "E9.5.2.7", {"center": v(27.5, 44.23) * mm, "radius": 4 * mm, "construction": true});
            skLineSegment(sketch, "E9.5.3.0", {"start": v(27.5, 18.85) * mm, "end": v(31.5, 16.54) * mm});
            skPoint(sketch, "E9.5.3.1", {"position": v(25.5, 17.7) * mm});
            skLineSegment(sketch, "E9.5.3.2", {"start": v(27.5, 9.61) * mm, "end": v(23.5, 11.92) * mm});
            skLineSegment(sketch, "E9.5.3.3", {"start": v(31.5, 11.92) * mm, "end": v(27.5, 9.61) * mm});
            skLineSegment(sketch, "E9.5.3.4", {"start": v(31.5, 16.54) * mm, "end": v(31.5, 11.92) * mm});
            skLineSegment(sketch, "E9.5.3.5", {"start": v(23.5, 11.92) * mm, "end": v(23.5, 16.54) * mm});
            skLineSegment(sketch, "E9.5.3.6", {"start": v(23.5, 16.54) * mm, "end": v(27.5, 18.85) * mm});
            skCircle(sketch, "E9.5.3.7", {"center": v(27.5, 14.23) * mm, "radius": 4 * mm, "construction": true});
            skLineSegment(sketch, "E9.5.4.0", {"start": v(27.5, -11.15) * mm, "end": v(31.5, -13.46) * mm});
            skPoint(sketch, "E9.5.4.1", {"position": v(25.5, -12.3) * mm});
            skLineSegment(sketch, "E9.5.4.2", {"start": v(27.5, -20.39) * mm, "end": v(23.5, -18.08) * mm});
            skLineSegment(sketch, "E9.5.4.3", {"start": v(31.5, -18.08) * mm, "end": v(27.5, -20.39) * mm});
            skLineSegment(sketch, "E9.5.4.4", {"start": v(31.5, -13.46) * mm, "end": v(31.5, -18.08) * mm});
            skLineSegment(sketch, "E9.5.4.5", {"start": v(23.5, -18.08) * mm, "end": v(23.5, -13.46) * mm});
            skLineSegment(sketch, "E9.5.4.6", {"start": v(23.5, -13.46) * mm, "end": v(27.5, -11.15) * mm});
            skCircle(sketch, "E9.5.4.7", {"center": v(27.5, -15.77) * mm, "radius": 4 * mm, "construction": true});
            skLineSegment(sketch, "E9.5.5.0", {"start": v(27.5, -41.15) * mm, "end": v(31.5, -43.46) * mm});
            skPoint(sketch, "E9.5.5.1", {"position": v(25.5, -42.3) * mm});
            skLineSegment(sketch, "E9.5.5.2", {"start": v(27.5, -50.39) * mm, "end": v(23.5, -48.08) * mm});
            skLineSegment(sketch, "E9.5.5.3", {"start": v(31.5, -48.08) * mm, "end": v(27.5, -50.39) * mm});
            skLineSegment(sketch, "E9.5.5.4", {"start": v(31.5, -43.46) * mm, "end": v(31.5, -48.08) * mm});
            skLineSegment(sketch, "E9.5.5.5", {"start": v(23.5, -48.08) * mm, "end": v(23.5, -43.46) * mm});
            skLineSegment(sketch, "E9.5.5.6", {"start": v(23.5, -43.46) * mm, "end": v(27.5, -41.15) * mm});
            skCircle(sketch, "E9.5.5.7", {"center": v(27.5, -45.77) * mm, "radius": 4 * mm, "construction": true});
            skLineSegment(sketch, "E9.5.6.0", {"start": v(27.5, -71.15) * mm, "end": v(31.5, -73.46) * mm});
            skPoint(sketch, "E9.5.6.1", {"position": v(25.5, -72.3) * mm});
            skLineSegment(sketch, "E9.5.6.2", {"start": v(27.5, -80.39) * mm, "end": v(23.5, -78.08) * mm});
            skLineSegment(sketch, "E9.5.6.3", {"start": v(31.5, -78.08) * mm, "end": v(27.5, -80.39) * mm});
            skLineSegment(sketch, "E9.5.6.4", {"start": v(31.5, -73.46) * mm, "end": v(31.5, -78.08) * mm});
            skLineSegment(sketch, "E9.5.6.5", {"start": v(23.5, -78.08) * mm, "end": v(23.5, -73.46) * mm});
            skLineSegment(sketch, "E9.5.6.6", {"start": v(23.5, -73.46) * mm, "end": v(27.5, -71.15) * mm});
            skCircle(sketch, "E9.5.6.7", {"center": v(27.5, -75.77) * mm, "radius": 4 * mm, "construction": true});
            skLineSegment(sketch, "E9.5.7.0", {"start": v(27.5, -101.15) * mm, "end": v(31.5, -103.46) * mm});
            skPoint(sketch, "E9.5.7.1", {"position": v(25.5, -102.3) * mm});
            skLineSegment(sketch, "E9.5.7.2", {"start": v(27.5, -110.39) * mm, "end": v(23.5, -108.08) * mm});
            skLineSegment(sketch, "E9.5.7.3", {"start": v(31.5, -108.08) * mm, "end": v(27.5, -110.39) * mm});
            skLineSegment(sketch, "E9.5.7.4", {"start": v(31.5, -103.46) * mm, "end": v(31.5, -108.08) * mm});
            skLineSegment(sketch, "E9.5.7.5", {"start": v(23.5, -108.08) * mm, "end": v(23.5, -103.46) * mm});
            skLineSegment(sketch, "E9.5.7.6", {"start": v(23.5, -103.46) * mm, "end": v(27.5, -101.15) * mm});
            skCircle(sketch, "E9.5.7.7", {"center": v(27.5, -105.77) * mm, "radius": 4 * mm, "construction": true});
            skLineSegment(sketch, "E9.6.0.0", {"start": v(57.5, 108.85) * mm, "end": v(61.5, 106.54) * mm});
            skPoint(sketch, "E9.6.0.1", {"position": v(55.5, 107.7) * mm});
            skLineSegment(sketch, "E9.6.0.2", {"start": v(57.5, 99.61) * mm, "end": v(53.5, 101.92) * mm});
            skLineSegment(sketch, "E9.6.0.3", {"start": v(61.5, 101.92) * mm, "end": v(57.5, 99.61) * mm});
            skLineSegment(sketch, "E9.6.0.4", {"start": v(61.5, 106.54) * mm, "end": v(61.5, 101.92) * mm});
            skLineSegment(sketch, "E9.6.0.5", {"start": v(53.5, 101.92) * mm, "end": v(53.5, 106.54) * mm});
            skLineSegment(sketch, "E9.6.0.6", {"start": v(53.5, 106.54) * mm, "end": v(57.5, 108.85) * mm});
            skCircle(sketch, "E9.6.0.7", {"center": v(57.5, 104.23) * mm, "radius": 4 * mm, "construction": true});
            skLineSegment(sketch, "E9.6.1.0", {"start": v(57.5, 78.85) * mm, "end": v(61.5, 76.54) * mm});
            skPoint(sketch, "E9.6.1.1", {"position": v(55.5, 77.7) * mm});
            skLineSegment(sketch, "E9.6.1.2", {"start": v(57.5, 69.61) * mm, "end": v(53.5, 71.92) * mm});
            skLineSegment(sketch, "E9.6.1.3", {"start": v(61.5, 71.92) * mm, "end": v(57.5, 69.61) * mm});
            skLineSegment(sketch, "E9.6.1.4", {"start": v(61.5, 76.54) * mm, "end": v(61.5, 71.92) * mm});
            skLineSegment(sketch, "E9.6.1.5", {"start": v(53.5, 71.92) * mm, "end": v(53.5, 76.54) * mm});
            skLineSegment(sketch, "E9.6.1.6", {"start": v(53.5, 76.54) * mm, "end": v(57.5, 78.85) * mm});
            skCircle(sketch, "E9.6.1.7", {"center": v(57.5, 74.23) * mm, "radius": 4 * mm, "construction": true});
            skLineSegment(sketch, "E9.6.2.0", {"start": v(57.5, 48.85) * mm, "end": v(61.5, 46.54) * mm});
            skPoint(sketch, "E9.6.2.1", {"position": v(55.5, 47.7) * mm});
            skLineSegment(sketch, "E9.6.2.2", {"start": v(57.5, 39.61) * mm, "end": v(53.5, 41.92) * mm});
            skLineSegment(sketch, "E9.6.2.3", {"start": v(61.5, 41.92) * mm, "end": v(57.5, 39.61) * mm});
            skLineSegment(sketch, "E9.6.2.4", {"start": v(61.5, 46.54) * mm, "end": v(61.5, 41.92) * mm});
            skLineSegment(sketch, "E9.6.2.5", {"start": v(53.5, 41.92) * mm, "end": v(53.5, 46.54) * mm});
            skLineSegment(sketch, "E9.6.2.6", {"start": v(53.5, 46.54) * mm, "end": v(57.5, 48.85) * mm});
            skCircle(sketch, "E9.6.2.7", {"center": v(57.5, 44.23) * mm, "radius": 4 * mm, "construction": true});
            skLineSegment(sketch, "E9.6.3.0", {"start": v(57.5, 18.85) * mm, "end": v(61.5, 16.54) * mm});
            skPoint(sketch, "E9.6.3.1", {"position": v(55.5, 17.7) * mm});
            skLineSegment(sketch, "E9.6.3.2", {"start": v(57.5, 9.61) * mm, "end": v(53.5, 11.92) * mm});
            skLineSegment(sketch, "E9.6.3.3", {"start": v(61.5, 11.92) * mm, "end": v(57.5, 9.61) * mm});
            skLineSegment(sketch, "E9.6.3.4", {"start": v(61.5, 16.54) * mm, "end": v(61.5, 11.92) * mm});
            skLineSegment(sketch, "E9.6.3.5", {"start": v(53.5, 11.92) * mm, "end": v(53.5, 16.54) * mm});
            skLineSegment(sketch, "E9.6.3.6", {"start": v(53.5, 16.54) * mm, "end": v(57.5, 18.85) * mm});
            skCircle(sketch, "E9.6.3.7", {"center": v(57.5, 14.23) * mm, "radius": 4 * mm, "construction": true});
            skLineSegment(sketch, "E9.6.4.0", {"start": v(57.5, -11.15) * mm, "end": v(61.5, -13.46) * mm});
            skPoint(sketch, "E9.6.4.1", {"position": v(55.5, -12.3) * mm});
            skLineSegment(sketch, "E9.6.4.2", {"start": v(57.5, -20.39) * mm, "end": v(53.5, -18.08) * mm});
            skLineSegment(sketch, "E9.6.4.3", {"start": v(61.5, -18.08) * mm, "end": v(57.5, -20.39) * mm});
            skLineSegment(sketch, "E9.6.4.4", {"start": v(61.5, -13.46) * mm, "end": v(61.5, -18.08) * mm});
            skLineSegment(sketch, "E9.6.4.5", {"start": v(53.5, -18.08) * mm, "end": v(53.5, -13.46) * mm});
            skLineSegment(sketch, "E9.6.4.6", {"start": v(53.5, -13.46) * mm, "end": v(57.5, -11.15) * mm});
            skCircle(sketch, "E9.6.4.7", {"center": v(57.5, -15.77) * mm, "radius": 4 * mm, "construction": true});
            skLineSegment(sketch, "E9.6.5.0", {"start": v(57.5, -41.15) * mm, "end": v(61.5, -43.46) * mm});
            skPoint(sketch, "E9.6.5.1", {"position": v(55.5, -42.3) * mm});
            skLineSegment(sketch, "E9.6.5.2", {"start": v(57.5, -50.39) * mm, "end": v(53.5, -48.08) * mm});
            skLineSegment(sketch, "E9.6.5.3", {"start": v(61.5, -48.08) * mm, "end": v(57.5, -50.39) * mm});
            skLineSegment(sketch, "E9.6.5.4", {"start": v(61.5, -43.46) * mm, "end": v(61.5, -48.08) * mm});
            skLineSegment(sketch, "E9.6.5.5", {"start": v(53.5, -48.08) * mm, "end": v(53.5, -43.46) * mm});
            skLineSegment(sketch, "E9.6.5.6", {"start": v(53.5, -43.46) * mm, "end": v(57.5, -41.15) * mm});
            skCircle(sketch, "E9.6.5.7", {"center": v(57.5, -45.77) * mm, "radius": 4 * mm, "construction": true});
            skLineSegment(sketch, "E9.6.6.0", {"start": v(57.5, -71.15) * mm, "end": v(61.5, -73.46) * mm});
            skPoint(sketch, "E9.6.6.1", {"position": v(55.5, -72.3) * mm});
            skLineSegment(sketch, "E9.6.6.2", {"start": v(57.5, -80.39) * mm, "end": v(53.5, -78.08) * mm});
            skLineSegment(sketch, "E9.6.6.3", {"start": v(61.5, -78.08) * mm, "end": v(57.5, -80.39) * mm});
            skLineSegment(sketch, "E9.6.6.4", {"start": v(61.5, -73.46) * mm, "end": v(61.5, -78.08) * mm});
            skLineSegment(sketch, "E9.6.6.5", {"start": v(53.5, -78.08) * mm, "end": v(53.5, -73.46) * mm});
            skLineSegment(sketch, "E9.6.6.6", {"start": v(53.5, -73.46) * mm, "end": v(57.5, -71.15) * mm});
            skCircle(sketch, "E9.6.6.7", {"center": v(57.5, -75.77) * mm, "radius": 4 * mm, "construction": true});
            skLineSegment(sketch, "E9.6.7.0", {"start": v(57.5, -101.15) * mm, "end": v(61.5, -103.46) * mm});
            skPoint(sketch, "E9.6.7.1", {"position": v(55.5, -102.3) * mm});
            skLineSegment(sketch, "E9.6.7.2", {"start": v(57.5, -110.39) * mm, "end": v(53.5, -108.08) * mm});
            skLineSegment(sketch, "E9.6.7.3", {"start": v(61.5, -108.08) * mm, "end": v(57.5, -110.39) * mm});
            skLineSegment(sketch, "E9.6.7.4", {"start": v(61.5, -103.46) * mm, "end": v(61.5, -108.08) * mm});
            skLineSegment(sketch, "E9.6.7.5", {"start": v(53.5, -108.08) * mm, "end": v(53.5, -103.46) * mm});
            skLineSegment(sketch, "E9.6.7.6", {"start": v(53.5, -103.46) * mm, "end": v(57.5, -101.15) * mm});
            skCircle(sketch, "E9.6.7.7", {"center": v(57.5, -105.77) * mm, "radius": 4 * mm, "construction": true});
            skLineSegment(sketch, "E9.7.0.0", {"start": v(87.5, 108.85) * mm, "end": v(91.5, 106.54) * mm});
            skPoint(sketch, "E9.7.0.1", {"position": v(85.5, 107.7) * mm});
            skLineSegment(sketch, "E9.7.0.2", {"start": v(87.5, 99.61) * mm, "end": v(83.5, 101.92) * mm});
            skLineSegment(sketch, "E9.7.0.3", {"start": v(91.5, 101.92) * mm, "end": v(87.5, 99.61) * mm});
            skLineSegment(sketch, "E9.7.0.4", {"start": v(91.5, 106.54) * mm, "end": v(91.5, 101.92) * mm});
            skLineSegment(sketch, "E9.7.0.5", {"start": v(83.5, 101.92) * mm, "end": v(83.5, 106.54) * mm});
            skLineSegment(sketch, "E9.7.0.6", {"start": v(83.5, 106.54) * mm, "end": v(87.5, 108.85) * mm});
            skCircle(sketch, "E9.7.0.7", {"center": v(87.5, 104.23) * mm, "radius": 4 * mm, "construction": true});
            skLineSegment(sketch, "E9.7.1.0", {"start": v(87.5, 78.85) * mm, "end": v(91.5, 76.54) * mm});
            skPoint(sketch, "E9.7.1.1", {"position": v(85.5, 77.7) * mm});
            skLineSegment(sketch, "E9.7.1.2", {"start": v(87.5, 69.61) * mm, "end": v(83.5, 71.92) * mm});
            skLineSegment(sketch, "E9.7.1.3", {"start": v(91.5, 71.92) * mm, "end": v(87.5, 69.61) * mm});
            skLineSegment(sketch, "E9.7.1.4", {"start": v(91.5, 76.54) * mm, "end": v(91.5, 71.92) * mm});
            skLineSegment(sketch, "E9.7.1.5", {"start": v(83.5, 71.92) * mm, "end": v(83.5, 76.54) * mm});
            skLineSegment(sketch, "E9.7.1.6", {"start": v(83.5, 76.54) * mm, "end": v(87.5, 78.85) * mm});
            skCircle(sketch, "E9.7.1.7", {"center": v(87.5, 74.23) * mm, "radius": 4 * mm, "construction": true});
            skLineSegment(sketch, "E9.7.2.0", {"start": v(87.5, 48.85) * mm, "end": v(91.5, 46.54) * mm});
            skPoint(sketch, "E9.7.2.1", {"position": v(85.5, 47.7) * mm});
            skLineSegment(sketch, "E9.7.2.2", {"start": v(87.5, 39.61) * mm, "end": v(83.5, 41.92) * mm});
            skLineSegment(sketch, "E9.7.2.3", {"start": v(91.5, 41.92) * mm, "end": v(87.5, 39.61) * mm});
            skLineSegment(sketch, "E9.7.2.4", {"start": v(91.5, 46.54) * mm, "end": v(91.5, 41.92) * mm});
            skLineSegment(sketch, "E9.7.2.5", {"start": v(83.5, 41.92) * mm, "end": v(83.5, 46.54) * mm});
            skLineSegment(sketch, "E9.7.2.6", {"start": v(83.5, 46.54) * mm, "end": v(87.5, 48.85) * mm});
            skCircle(sketch, "E9.7.2.7", {"center": v(87.5, 44.23) * mm, "radius": 4 * mm, "construction": true});
            skLineSegment(sketch, "E9.7.3.0", {"start": v(87.5, 18.85) * mm, "end": v(91.5, 16.54) * mm});
            skPoint(sketch, "E9.7.3.1", {"position": v(85.5, 17.7) * mm});
            skLineSegment(sketch, "E9.7.3.2", {"start": v(87.5, 9.61) * mm, "end": v(83.5, 11.92) * mm});
            skLineSegment(sketch, "E9.7.3.3", {"start": v(91.5, 11.92) * mm, "end": v(87.5, 9.61) * mm});
            skLineSegment(sketch, "E9.7.3.4", {"start": v(91.5, 16.54) * mm, "end": v(91.5, 11.92) * mm});
            skLineSegment(sketch, "E9.7.3.5", {"start": v(83.5, 11.92) * mm, "end": v(83.5, 16.54) * mm});
            skLineSegment(sketch, "E9.7.3.6", {"start": v(83.5, 16.54) * mm, "end": v(87.5, 18.85) * mm});
            skCircle(sketch, "E9.7.3.7", {"center": v(87.5, 14.23) * mm, "radius": 4 * mm, "construction": true});
            skLineSegment(sketch, "E9.7.4.0", {"start": v(87.5, -11.15) * mm, "end": v(91.5, -13.46) * mm});
            skPoint(sketch, "E9.7.4.1", {"position": v(85.5, -12.3) * mm});
            skLineSegment(sketch, "E9.7.4.2", {"start": v(87.5, -20.39) * mm, "end": v(83.5, -18.08) * mm});
            skLineSegment(sketch, "E9.7.4.3", {"start": v(91.5, -18.08) * mm, "end": v(87.5, -20.39) * mm});
            skLineSegment(sketch, "E9.7.4.4", {"start": v(91.5, -13.46) * mm, "end": v(91.5, -18.08) * mm});
            skLineSegment(sketch, "E9.7.4.5", {"start": v(83.5, -18.08) * mm, "end": v(83.5, -13.46) * mm});
            skLineSegment(sketch, "E9.7.4.6", {"start": v(83.5, -13.46) * mm, "end": v(87.5, -11.15) * mm});
            skCircle(sketch, "E9.7.4.7", {"center": v(87.5, -15.77) * mm, "radius": 4 * mm, "construction": true});
            skLineSegment(sketch, "E9.7.5.0", {"start": v(87.5, -41.15) * mm, "end": v(91.5, -43.46) * mm});
            skPoint(sketch, "E9.7.5.1", {"position": v(85.5, -42.3) * mm});
            skLineSegment(sketch, "E9.7.5.2", {"start": v(87.5, -50.39) * mm, "end": v(83.5, -48.08) * mm});
            skLineSegment(sketch, "E9.7.5.3", {"start": v(91.5, -48.08) * mm, "end": v(87.5, -50.39) * mm});
            skLineSegment(sketch, "E9.7.5.4", {"start": v(91.5, -43.46) * mm, "end": v(91.5, -48.08) * mm});
            skLineSegment(sketch, "E9.7.5.5", {"start": v(83.5, -48.08) * mm, "end": v(83.5, -43.46) * mm});
            skLineSegment(sketch, "E9.7.5.6", {"start": v(83.5, -43.46) * mm, "end": v(87.5, -41.15) * mm});
            skCircle(sketch, "E9.7.5.7", {"center": v(87.5, -45.77) * mm, "radius": 4 * mm, "construction": true});
            skLineSegment(sketch, "E9.7.6.0", {"start": v(87.5, -71.15) * mm, "end": v(91.5, -73.46) * mm});
            skPoint(sketch, "E9.7.6.1", {"position": v(85.5, -72.3) * mm});
            skLineSegment(sketch, "E9.7.6.2", {"start": v(87.5, -80.39) * mm, "end": v(83.5, -78.08) * mm});
            skLineSegment(sketch, "E9.7.6.3", {"start": v(91.5, -78.08) * mm, "end": v(87.5, -80.39) * mm});
            skLineSegment(sketch, "E9.7.6.4", {"start": v(91.5, -73.46) * mm, "end": v(91.5, -78.08) * mm});
            skLineSegment(sketch, "E9.7.6.5", {"start": v(83.5, -78.08) * mm, "end": v(83.5, -73.46) * mm});
            skLineSegment(sketch, "E9.7.6.6", {"start": v(83.5, -73.46) * mm, "end": v(87.5, -71.15) * mm});
            skCircle(sketch, "E9.7.6.7", {"center": v(87.5, -75.77) * mm, "radius": 4 * mm, "construction": true});
            skLineSegment(sketch, "E9.7.7.0", {"start": v(87.5, -101.15) * mm, "end": v(91.5, -103.46) * mm});
            skPoint(sketch, "E9.7.7.1", {"position": v(85.5, -102.3) * mm});
            skLineSegment(sketch, "E9.7.7.2", {"start": v(87.5, -110.39) * mm, "end": v(83.5, -108.08) * mm});
            skLineSegment(sketch, "E9.7.7.3", {"start": v(91.5, -108.08) * mm, "end": v(87.5, -110.39) * mm});
            skLineSegment(sketch, "E9.7.7.4", {"start": v(91.5, -103.46) * mm, "end": v(91.5, -108.08) * mm});
            skLineSegment(sketch, "E9.7.7.5", {"start": v(83.5, -108.08) * mm, "end": v(83.5, -103.46) * mm});
            skLineSegment(sketch, "E9.7.7.6", {"start": v(83.5, -103.46) * mm, "end": v(87.5, -101.15) * mm});
            skCircle(sketch, "E9.7.7.7", {"center": v(87.5, -105.77) * mm, "radius": 4 * mm, "construction": true});
            skLineSegment(sketch, "E9.8.0.0", {"start": v(117.5, 108.85) * mm, "end": v(121.5, 106.54) * mm});
            skPoint(sketch, "E9.8.0.1", {"position": v(115.5, 107.7) * mm});
            skLineSegment(sketch, "E9.8.0.2", {"start": v(117.5, 99.61) * mm, "end": v(113.5, 101.92) * mm});
            skLineSegment(sketch, "E9.8.0.3", {"start": v(121.5, 101.92) * mm, "end": v(117.5, 99.61) * mm});
            skLineSegment(sketch, "E9.8.0.4", {"start": v(121.5, 106.54) * mm, "end": v(121.5, 101.92) * mm});
            skLineSegment(sketch, "E9.8.0.5", {"start": v(113.5, 101.92) * mm, "end": v(113.5, 106.54) * mm});
            skLineSegment(sketch, "E9.8.0.6", {"start": v(113.5, 106.54) * mm, "end": v(117.5, 108.85) * mm});
            skCircle(sketch, "E9.8.0.7", {"center": v(117.5, 104.23) * mm, "radius": 4 * mm, "construction": true});
            skLineSegment(sketch, "E9.8.1.0", {"start": v(117.5, 78.85) * mm, "end": v(121.5, 76.54) * mm});
            skPoint(sketch, "E9.8.1.1", {"position": v(115.5, 77.7) * mm});
            skLineSegment(sketch, "E9.8.1.2", {"start": v(117.5, 69.61) * mm, "end": v(113.5, 71.92) * mm});
            skLineSegment(sketch, "E9.8.1.3", {"start": v(121.5, 71.92) * mm, "end": v(117.5, 69.61) * mm});
            skLineSegment(sketch, "E9.8.1.4", {"start": v(121.5, 76.54) * mm, "end": v(121.5, 71.92) * mm});
            skLineSegment(sketch, "E9.8.1.5", {"start": v(113.5, 71.92) * mm, "end": v(113.5, 76.54) * mm});
            skLineSegment(sketch, "E9.8.1.6", {"start": v(113.5, 76.54) * mm, "end": v(117.5, 78.85) * mm});
            skCircle(sketch, "E9.8.1.7", {"center": v(117.5, 74.23) * mm, "radius": 4 * mm, "construction": true});
            skLineSegment(sketch, "E9.8.2.0", {"start": v(117.5, 48.85) * mm, "end": v(121.5, 46.54) * mm});
            skPoint(sketch, "E9.8.2.1", {"position": v(115.5, 47.7) * mm});
            skLineSegment(sketch, "E9.8.2.2", {"start": v(117.5, 39.61) * mm, "end": v(113.5, 41.92) * mm});
            skLineSegment(sketch, "E9.8.2.3", {"start": v(121.5, 41.92) * mm, "end": v(117.5, 39.61) * mm});
            skLineSegment(sketch, "E9.8.2.4", {"start": v(121.5, 46.54) * mm, "end": v(121.5, 41.92) * mm});
            skLineSegment(sketch, "E9.8.2.5", {"start": v(113.5, 41.92) * mm, "end": v(113.5, 46.54) * mm});
            skLineSegment(sketch, "E9.8.2.6", {"start": v(113.5, 46.54) * mm, "end": v(117.5, 48.85) * mm});
            skCircle(sketch, "E9.8.2.7", {"center": v(117.5, 44.23) * mm, "radius": 4 * mm, "construction": true});
            skLineSegment(sketch, "E9.8.3.0", {"start": v(117.5, 18.85) * mm, "end": v(121.5, 16.54) * mm});
            skPoint(sketch, "E9.8.3.1", {"position": v(115.5, 17.7) * mm});
            skLineSegment(sketch, "E9.8.3.2", {"start": v(117.5, 9.61) * mm, "end": v(113.5, 11.92) * mm});
            skLineSegment(sketch, "E9.8.3.3", {"start": v(121.5, 11.92) * mm, "end": v(117.5, 9.61) * mm});
            skLineSegment(sketch, "E9.8.3.4", {"start": v(121.5, 16.54) * mm, "end": v(121.5, 11.92) * mm});
            skLineSegment(sketch, "E9.8.3.5", {"start": v(113.5, 11.92) * mm, "end": v(113.5, 16.54) * mm});
            skLineSegment(sketch, "E9.8.3.6", {"start": v(113.5, 16.54) * mm, "end": v(117.5, 18.85) * mm});
            skCircle(sketch, "E9.8.3.7", {"center": v(117.5, 14.23) * mm, "radius": 4 * mm, "construction": true});
            skLineSegment(sketch, "E9.8.4.0", {"start": v(117.5, -11.15) * mm, "end": v(121.5, -13.46) * mm});
            skPoint(sketch, "E9.8.4.1", {"position": v(115.5, -12.3) * mm});
            skLineSegment(sketch, "E9.8.4.2", {"start": v(117.5, -20.39) * mm, "end": v(113.5, -18.08) * mm});
            skLineSegment(sketch, "E9.8.4.3", {"start": v(121.5, -18.08) * mm, "end": v(117.5, -20.39) * mm});
            skLineSegment(sketch, "E9.8.4.4", {"start": v(121.5, -13.46) * mm, "end": v(121.5, -18.08) * mm});
            skLineSegment(sketch, "E9.8.4.5", {"start": v(113.5, -18.08) * mm, "end": v(113.5, -13.46) * mm});
            skLineSegment(sketch, "E9.8.4.6", {"start": v(113.5, -13.46) * mm, "end": v(117.5, -11.15) * mm});
            skCircle(sketch, "E9.8.4.7", {"center": v(117.5, -15.77) * mm, "radius": 4 * mm, "construction": true});
            skLineSegment(sketch, "E9.8.5.0", {"start": v(117.5, -41.15) * mm, "end": v(121.5, -43.46) * mm});
            skPoint(sketch, "E9.8.5.1", {"position": v(115.5, -42.3) * mm});
            skLineSegment(sketch, "E9.8.5.2", {"start": v(117.5, -50.39) * mm, "end": v(113.5, -48.08) * mm});
            skLineSegment(sketch, "E9.8.5.3", {"start": v(121.5, -48.08) * mm, "end": v(117.5, -50.39) * mm});
            skLineSegment(sketch, "E9.8.5.4", {"start": v(121.5, -43.46) * mm, "end": v(121.5, -48.08) * mm});
            skLineSegment(sketch, "E9.8.5.5", {"start": v(113.5, -48.08) * mm, "end": v(113.5, -43.46) * mm});
            skLineSegment(sketch, "E9.8.5.6", {"start": v(113.5, -43.46) * mm, "end": v(117.5, -41.15) * mm});
            skCircle(sketch, "E9.8.5.7", {"center": v(117.5, -45.77) * mm, "radius": 4 * mm, "construction": true});
            skLineSegment(sketch, "E9.8.6.0", {"start": v(117.5, -71.15) * mm, "end": v(121.5, -73.46) * mm});
            skPoint(sketch, "E9.8.6.1", {"position": v(115.5, -72.3) * mm});
            skLineSegment(sketch, "E9.8.6.2", {"start": v(117.5, -80.39) * mm, "end": v(113.5, -78.08) * mm});
            skLineSegment(sketch, "E9.8.6.3", {"start": v(121.5, -78.08) * mm, "end": v(117.5, -80.39) * mm});
            skLineSegment(sketch, "E9.8.6.4", {"start": v(121.5, -73.46) * mm, "end": v(121.5, -78.08) * mm});
            skLineSegment(sketch, "E9.8.6.5", {"start": v(113.5, -78.08) * mm, "end": v(113.5, -73.46) * mm});
            skLineSegment(sketch, "E9.8.6.6", {"start": v(113.5, -73.46) * mm, "end": v(117.5, -71.15) * mm});
            skCircle(sketch, "E9.8.6.7", {"center": v(117.5, -75.77) * mm, "radius": 4 * mm, "construction": true});
            skLineSegment(sketch, "E9.8.7.0", {"start": v(117.5, -101.15) * mm, "end": v(121.5, -103.46) * mm});
            skPoint(sketch, "E9.8.7.1", {"position": v(115.5, -102.3) * mm});
            skLineSegment(sketch, "E9.8.7.2", {"start": v(117.5, -110.39) * mm, "end": v(113.5, -108.08) * mm});
            skLineSegment(sketch, "E9.8.7.3", {"start": v(121.5, -108.08) * mm, "end": v(117.5, -110.39) * mm});
            skLineSegment(sketch, "E9.8.7.4", {"start": v(121.5, -103.46) * mm, "end": v(121.5, -108.08) * mm});
            skLineSegment(sketch, "E9.8.7.5", {"start": v(113.5, -108.08) * mm, "end": v(113.5, -103.46) * mm});
            skLineSegment(sketch, "E9.8.7.6", {"start": v(113.5, -103.46) * mm, "end": v(117.5, -101.15) * mm});
            skCircle(sketch, "E9.8.7.7", {"center": v(117.5, -105.77) * mm, "radius": 4 * mm, "construction": true});
            skLineSegment(sketch, "E9.direction1", {"start": v(-126.5, 101.92) * mm, "end": v(-96.5, 101.92) * mm, "construction": true});
            skLineSegment(sketch, "E9.direction2", {"start": v(-126.5, 101.92) * mm, "end": v(-126.5, 71.92) * mm, "construction": true});
            skLineSegment(sketch, "E10.0.0.8", {"start": v(-122.5, -131.15) * mm, "end": v(-118.5, -133.46) * mm});
            skPoint(sketch, "E10.3.0.8", {"position": v(-124.5, -132.3) * mm});
            skLineSegment(sketch, "E10.4.0.8", {"start": v(-122.5, -140.39) * mm, "end": v(-126.5, -138.08) * mm});
            skLineSegment(sketch, "E10.7.0.8", {"start": v(-118.5, -138.08) * mm, "end": v(-122.5, -140.39) * mm});
            skLineSegment(sketch, "E10.10.0.8", {"start": v(-118.5, -133.46) * mm, "end": v(-118.5, -138.08) * mm});
            skLineSegment(sketch, "E10.13.0.8", {"start": v(-126.5, -138.08) * mm, "end": v(-126.5, -133.46) * mm});
            skLineSegment(sketch, "E10.16.0.8", {"start": v(-126.5, -133.46) * mm, "end": v(-122.5, -131.15) * mm});
            skCircle(sketch, "E10.19.0.8", {"center": v(-122.5, -135.77) * mm, "radius": 4 * mm, "construction": true});
            skLineSegment(sketch, "E10.0.1.8", {"start": v(-92.5, -131.15) * mm, "end": v(-88.5, -133.46) * mm});
            skPoint(sketch, "E10.3.1.8", {"position": v(-94.5, -132.3) * mm});
            skLineSegment(sketch, "E10.4.1.8", {"start": v(-92.5, -140.39) * mm, "end": v(-96.5, -138.08) * mm});
            skLineSegment(sketch, "E10.7.1.8", {"start": v(-88.5, -138.08) * mm, "end": v(-92.5, -140.39) * mm});
            skLineSegment(sketch, "E10.10.1.8", {"start": v(-88.5, -133.46) * mm, "end": v(-88.5, -138.08) * mm});
            skLineSegment(sketch, "E10.13.1.8", {"start": v(-96.5, -138.08) * mm, "end": v(-96.5, -133.46) * mm});
            skLineSegment(sketch, "E10.16.1.8", {"start": v(-96.5, -133.46) * mm, "end": v(-92.5, -131.15) * mm});
            skCircle(sketch, "E10.19.1.8", {"center": v(-92.5, -135.77) * mm, "radius": 4 * mm, "construction": true});
            skLineSegment(sketch, "E10.0.2.8", {"start": v(-62.5, -131.15) * mm, "end": v(-58.5, -133.46) * mm});
            skPoint(sketch, "E10.3.2.8", {"position": v(-64.5, -132.3) * mm});
            skLineSegment(sketch, "E10.4.2.8", {"start": v(-62.5, -140.39) * mm, "end": v(-66.5, -138.08) * mm});
            skLineSegment(sketch, "E10.7.2.8", {"start": v(-58.5, -138.08) * mm, "end": v(-62.5, -140.39) * mm});
            skLineSegment(sketch, "E10.10.2.8", {"start": v(-58.5, -133.46) * mm, "end": v(-58.5, -138.08) * mm});
            skLineSegment(sketch, "E10.13.2.8", {"start": v(-66.5, -138.08) * mm, "end": v(-66.5, -133.46) * mm});
            skLineSegment(sketch, "E10.16.2.8", {"start": v(-66.5, -133.46) * mm, "end": v(-62.5, -131.15) * mm});
            skCircle(sketch, "E10.19.2.8", {"center": v(-62.5, -135.77) * mm, "radius": 4 * mm, "construction": true});
            skLineSegment(sketch, "E10.0.3.8", {"start": v(-32.5, -131.15) * mm, "end": v(-28.5, -133.46) * mm});
            skPoint(sketch, "E10.3.3.8", {"position": v(-34.5, -132.3) * mm});
            skLineSegment(sketch, "E10.4.3.8", {"start": v(-32.5, -140.39) * mm, "end": v(-36.5, -138.08) * mm});
            skLineSegment(sketch, "E10.7.3.8", {"start": v(-28.5, -138.08) * mm, "end": v(-32.5, -140.39) * mm});
            skLineSegment(sketch, "E10.10.3.8", {"start": v(-28.5, -133.46) * mm, "end": v(-28.5, -138.08) * mm});
            skLineSegment(sketch, "E10.13.3.8", {"start": v(-36.5, -138.08) * mm, "end": v(-36.5, -133.46) * mm});
            skLineSegment(sketch, "E10.16.3.8", {"start": v(-36.5, -133.46) * mm, "end": v(-32.5, -131.15) * mm});
            skCircle(sketch, "E10.19.3.8", {"center": v(-32.5, -135.77) * mm, "radius": 4 * mm, "construction": true});
            skLineSegment(sketch, "E10.0.4.8", {"start": v(-2.5, -131.15) * mm, "end": v(1.5, -133.46) * mm});
            skPoint(sketch, "E10.3.4.8", {"position": v(-4.5, -132.3) * mm});
            skLineSegment(sketch, "E10.4.4.8", {"start": v(-2.5, -140.39) * mm, "end": v(-6.5, -138.08) * mm});
            skLineSegment(sketch, "E10.7.4.8", {"start": v(1.5, -138.08) * mm, "end": v(-2.5, -140.39) * mm});
            skLineSegment(sketch, "E10.10.4.8", {"start": v(1.5, -133.46) * mm, "end": v(1.5, -138.08) * mm});
            skLineSegment(sketch, "E10.13.4.8", {"start": v(-6.5, -138.08) * mm, "end": v(-6.5, -133.46) * mm});
            skLineSegment(sketch, "E10.16.4.8", {"start": v(-6.5, -133.46) * mm, "end": v(-2.5, -131.15) * mm});
            skCircle(sketch, "E10.19.4.8", {"center": v(-2.5, -135.77) * mm, "radius": 4 * mm, "construction": true});
            skLineSegment(sketch, "E10.0.5.8", {"start": v(27.5, -131.15) * mm, "end": v(31.5, -133.46) * mm});
            skPoint(sketch, "E10.3.5.8", {"position": v(25.5, -132.3) * mm});
            skLineSegment(sketch, "E10.4.5.8", {"start": v(27.5, -140.39) * mm, "end": v(23.5, -138.08) * mm});
            skLineSegment(sketch, "E10.7.5.8", {"start": v(31.5, -138.08) * mm, "end": v(27.5, -140.39) * mm});
            skLineSegment(sketch, "E10.10.5.8", {"start": v(31.5, -133.46) * mm, "end": v(31.5, -138.08) * mm});
            skLineSegment(sketch, "E10.13.5.8", {"start": v(23.5, -138.08) * mm, "end": v(23.5, -133.46) * mm});
            skLineSegment(sketch, "E10.16.5.8", {"start": v(23.5, -133.46) * mm, "end": v(27.5, -131.15) * mm});
            skCircle(sketch, "E10.19.5.8", {"center": v(27.5, -135.77) * mm, "radius": 4 * mm, "construction": true});
            skLineSegment(sketch, "E10.0.6.8", {"start": v(57.5, -131.15) * mm, "end": v(61.5, -133.46) * mm});
            skPoint(sketch, "E10.3.6.8", {"position": v(55.5, -132.3) * mm});
            skLineSegment(sketch, "E10.4.6.8", {"start": v(57.5, -140.39) * mm, "end": v(53.5, -138.08) * mm});
            skLineSegment(sketch, "E10.7.6.8", {"start": v(61.5, -138.08) * mm, "end": v(57.5, -140.39) * mm});
            skLineSegment(sketch, "E10.10.6.8", {"start": v(61.5, -133.46) * mm, "end": v(61.5, -138.08) * mm});
            skLineSegment(sketch, "E10.13.6.8", {"start": v(53.5, -138.08) * mm, "end": v(53.5, -133.46) * mm});
            skLineSegment(sketch, "E10.16.6.8", {"start": v(53.5, -133.46) * mm, "end": v(57.5, -131.15) * mm});
            skCircle(sketch, "E10.19.6.8", {"center": v(57.5, -135.77) * mm, "radius": 4 * mm, "construction": true});
            skLineSegment(sketch, "E10.0.7.8", {"start": v(87.5, -131.15) * mm, "end": v(91.5, -133.46) * mm});
            skPoint(sketch, "E10.3.7.8", {"position": v(85.5, -132.3) * mm});
            skLineSegment(sketch, "E10.4.7.8", {"start": v(87.5, -140.39) * mm, "end": v(83.5, -138.08) * mm});
            skLineSegment(sketch, "E10.7.7.8", {"start": v(91.5, -138.08) * mm, "end": v(87.5, -140.39) * mm});
            skLineSegment(sketch, "E10.10.7.8", {"start": v(91.5, -133.46) * mm, "end": v(91.5, -138.08) * mm});
            skLineSegment(sketch, "E10.13.7.8", {"start": v(83.5, -138.08) * mm, "end": v(83.5, -133.46) * mm});
            skLineSegment(sketch, "E10.16.7.8", {"start": v(83.5, -133.46) * mm, "end": v(87.5, -131.15) * mm});
            skCircle(sketch, "E10.19.7.8", {"center": v(87.5, -135.77) * mm, "radius": 4 * mm, "construction": true});
            skLineSegment(sketch, "E10.0.8.8", {"start": v(117.5, -131.15) * mm, "end": v(121.5, -133.46) * mm});
            skPoint(sketch, "E10.3.8.8", {"position": v(115.5, -132.3) * mm});
            skLineSegment(sketch, "E10.4.8.8", {"start": v(117.5, -140.39) * mm, "end": v(113.5, -138.08) * mm});
            skLineSegment(sketch, "E10.7.8.8", {"start": v(121.5, -138.08) * mm, "end": v(117.5, -140.39) * mm});
            skLineSegment(sketch, "E10.10.8.8", {"start": v(121.5, -133.46) * mm, "end": v(121.5, -138.08) * mm});
            skLineSegment(sketch, "E10.13.8.8", {"start": v(113.5, -138.08) * mm, "end": v(113.5, -133.46) * mm});
            skLineSegment(sketch, "E10.16.8.8", {"start": v(113.5, -133.46) * mm, "end": v(117.5, -131.15) * mm});
            skCircle(sketch, "E10.19.8.8", {"center": v(117.5, -135.77) * mm, "radius": 4 * mm, "construction": true});
            skCircle(sketch, "E11.cCircle", {"center": v(-122.5, -160.77) * mm, "radius": 4 * mm, "construction": true});
            skLineSegment(sketch, "E11.0", {"start": v(-118.5, -163.08) * mm, "end": v(-122.5, -165.39) * mm});
            skLineSegment(sketch, "E11.1", {"start": v(-122.5, -165.39) * mm, "end": v(-126.5, -163.08) * mm});
            skLineSegment(sketch, "E11.2", {"start": v(-126.5, -163.08) * mm, "end": v(-126.5, -158.46) * mm});
            skLineSegment(sketch, "E11.3", {"start": v(-126.5, -158.46) * mm, "end": v(-122.5, -156.15) * mm});
            skLineSegment(sketch, "E11.4", {"start": v(-122.5, -156.15) * mm, "end": v(-118.5, -158.46) * mm});
            skLineSegment(sketch, "E11.5", {"start": v(-118.5, -158.46) * mm, "end": v(-118.5, -163.08) * mm});
            skPoint(sketch, "E11.0.midPoint", {"position": v(-120.5, -164.23) * mm});
            skPoint(sketch, "E12.1.0.0", {"position": v(-90.5, -164.23) * mm});
            skCircle(sketch, "E12.1.0.1", {"center": v(-92.5, -160.77) * mm, "radius": 4 * mm, "construction": true});
            skLineSegment(sketch, "E12.1.0.2", {"start": v(-96.5, -163.08) * mm, "end": v(-96.5, -158.46) * mm});
            skLineSegment(sketch, "E12.1.0.3", {"start": v(-88.5, -158.46) * mm, "end": v(-88.5, -163.08) * mm});
            skLineSegment(sketch, "E12.1.0.4", {"start": v(-88.5, -163.08) * mm, "end": v(-92.5, -165.39) * mm});
            skLineSegment(sketch, "E12.1.0.5", {"start": v(-92.5, -165.39) * mm, "end": v(-96.5, -163.08) * mm});
            skLineSegment(sketch, "E12.1.0.6", {"start": v(-92.5, -156.15) * mm, "end": v(-88.5, -158.46) * mm});
            skLineSegment(sketch, "E12.1.0.7", {"start": v(-96.5, -158.46) * mm, "end": v(-92.5, -156.15) * mm});
            skPoint(sketch, "E12.2.0.0", {"position": v(-60.5, -164.23) * mm});
            skCircle(sketch, "E12.2.0.1", {"center": v(-62.5, -160.77) * mm, "radius": 4 * mm, "construction": true});
            skLineSegment(sketch, "E12.2.0.2", {"start": v(-66.5, -163.08) * mm, "end": v(-66.5, -158.46) * mm});
            skLineSegment(sketch, "E12.2.0.3", {"start": v(-58.5, -158.46) * mm, "end": v(-58.5, -163.08) * mm});
            skLineSegment(sketch, "E12.2.0.4", {"start": v(-58.5, -163.08) * mm, "end": v(-62.5, -165.39) * mm});
            skLineSegment(sketch, "E12.2.0.5", {"start": v(-62.5, -165.39) * mm, "end": v(-66.5, -163.08) * mm});
            skLineSegment(sketch, "E12.2.0.6", {"start": v(-62.5, -156.15) * mm, "end": v(-58.5, -158.46) * mm});
            skLineSegment(sketch, "E12.2.0.7", {"start": v(-66.5, -158.46) * mm, "end": v(-62.5, -156.15) * mm});
            skPoint(sketch, "E12.3.0.0", {"position": v(-30.5, -164.23) * mm});
            skCircle(sketch, "E12.3.0.1", {"center": v(-32.5, -160.77) * mm, "radius": 4 * mm, "construction": true});
            skLineSegment(sketch, "E12.3.0.2", {"start": v(-36.5, -163.08) * mm, "end": v(-36.5, -158.46) * mm});
            skLineSegment(sketch, "E12.3.0.3", {"start": v(-28.5, -158.46) * mm, "end": v(-28.5, -163.08) * mm});
            skLineSegment(sketch, "E12.3.0.4", {"start": v(-28.5, -163.08) * mm, "end": v(-32.5, -165.39) * mm});
            skLineSegment(sketch, "E12.3.0.5", {"start": v(-32.5, -165.39) * mm, "end": v(-36.5, -163.08) * mm});
            skLineSegment(sketch, "E12.3.0.6", {"start": v(-32.5, -156.15) * mm, "end": v(-28.5, -158.46) * mm});
            skLineSegment(sketch, "E12.3.0.7", {"start": v(-36.5, -158.46) * mm, "end": v(-32.5, -156.15) * mm});
            skPoint(sketch, "E12.4.0.0", {"position": v(-0.5, -164.23) * mm});
            skCircle(sketch, "E12.4.0.1", {"center": v(-2.5, -160.77) * mm, "radius": 4 * mm, "construction": true});
            skLineSegment(sketch, "E12.4.0.2", {"start": v(-6.5, -163.08) * mm, "end": v(-6.5, -158.46) * mm});
            skLineSegment(sketch, "E12.4.0.3", {"start": v(1.5, -158.46) * mm, "end": v(1.5, -163.08) * mm});
            skLineSegment(sketch, "E12.4.0.4", {"start": v(1.5, -163.08) * mm, "end": v(-2.5, -165.39) * mm});
            skLineSegment(sketch, "E12.4.0.5", {"start": v(-2.5, -165.39) * mm, "end": v(-6.5, -163.08) * mm});
            skLineSegment(sketch, "E12.4.0.6", {"start": v(-2.5, -156.15) * mm, "end": v(1.5, -158.46) * mm});
            skLineSegment(sketch, "E12.4.0.7", {"start": v(-6.5, -158.46) * mm, "end": v(-2.5, -156.15) * mm});
            skPoint(sketch, "E12.5.0.0", {"position": v(29.5, -164.23) * mm});
            skCircle(sketch, "E12.5.0.1", {"center": v(27.5, -160.77) * mm, "radius": 4 * mm, "construction": true});
            skLineSegment(sketch, "E12.5.0.2", {"start": v(23.5, -163.08) * mm, "end": v(23.5, -158.46) * mm});
            skLineSegment(sketch, "E12.5.0.3", {"start": v(31.5, -158.46) * mm, "end": v(31.5, -163.08) * mm});
            skLineSegment(sketch, "E12.5.0.4", {"start": v(31.5, -163.08) * mm, "end": v(27.5, -165.39) * mm});
            skLineSegment(sketch, "E12.5.0.5", {"start": v(27.5, -165.39) * mm, "end": v(23.5, -163.08) * mm});
            skLineSegment(sketch, "E12.5.0.6", {"start": v(27.5, -156.15) * mm, "end": v(31.5, -158.46) * mm});
            skLineSegment(sketch, "E12.5.0.7", {"start": v(23.5, -158.46) * mm, "end": v(27.5, -156.15) * mm});
            skPoint(sketch, "E12.6.0.0", {"position": v(59.5, -164.23) * mm});
            skCircle(sketch, "E12.6.0.1", {"center": v(57.5, -160.77) * mm, "radius": 4 * mm, "construction": true});
            skLineSegment(sketch, "E12.6.0.2", {"start": v(53.5, -163.08) * mm, "end": v(53.5, -158.46) * mm});
            skLineSegment(sketch, "E12.6.0.3", {"start": v(61.5, -158.46) * mm, "end": v(61.5, -163.08) * mm});
            skLineSegment(sketch, "E12.6.0.4", {"start": v(61.5, -163.08) * mm, "end": v(57.5, -165.39) * mm});
            skLineSegment(sketch, "E12.6.0.5", {"start": v(57.5, -165.39) * mm, "end": v(53.5, -163.08) * mm});
            skLineSegment(sketch, "E12.6.0.6", {"start": v(57.5, -156.15) * mm, "end": v(61.5, -158.46) * mm});
            skLineSegment(sketch, "E12.6.0.7", {"start": v(53.5, -158.46) * mm, "end": v(57.5, -156.15) * mm});
            skPoint(sketch, "E12.7.0.0", {"position": v(89.5, -164.23) * mm});
            skCircle(sketch, "E12.7.0.1", {"center": v(87.5, -160.77) * mm, "radius": 4 * mm, "construction": true});
            skLineSegment(sketch, "E12.7.0.2", {"start": v(83.5, -163.08) * mm, "end": v(83.5, -158.46) * mm});
            skLineSegment(sketch, "E12.7.0.3", {"start": v(91.5, -158.46) * mm, "end": v(91.5, -163.08) * mm});
            skLineSegment(sketch, "E12.7.0.4", {"start": v(91.5, -163.08) * mm, "end": v(87.5, -165.39) * mm});
            skLineSegment(sketch, "E12.7.0.5", {"start": v(87.5, -165.39) * mm, "end": v(83.5, -163.08) * mm});
            skLineSegment(sketch, "E12.7.0.6", {"start": v(87.5, -156.15) * mm, "end": v(91.5, -158.46) * mm});
            skLineSegment(sketch, "E12.7.0.7", {"start": v(83.5, -158.46) * mm, "end": v(87.5, -156.15) * mm});
            skPoint(sketch, "E12.8.0.0", {"position": v(119.5, -164.23) * mm});
            skCircle(sketch, "E12.8.0.1", {"center": v(117.5, -160.77) * mm, "radius": 4 * mm, "construction": true});
            skLineSegment(sketch, "E12.8.0.2", {"start": v(113.5, -163.08) * mm, "end": v(113.5, -158.46) * mm});
            skLineSegment(sketch, "E12.8.0.3", {"start": v(121.5, -158.46) * mm, "end": v(121.5, -163.08) * mm});
            skLineSegment(sketch, "E12.8.0.4", {"start": v(121.5, -163.08) * mm, "end": v(117.5, -165.39) * mm});
            skLineSegment(sketch, "E12.8.0.5", {"start": v(117.5, -165.39) * mm, "end": v(113.5, -163.08) * mm});
            skLineSegment(sketch, "E12.8.0.6", {"start": v(117.5, -156.15) * mm, "end": v(121.5, -158.46) * mm});
            skLineSegment(sketch, "E12.8.0.7", {"start": v(113.5, -158.46) * mm, "end": v(117.5, -156.15) * mm});
            skLineSegment(sketch, "E12.direction1", {"start": v(-126.5, -163.08) * mm, "end": v(-96.5, -163.08) * mm, "construction": true});
            skLineSegment(sketch, "E13.MirrorCS", {"start": v(-92.5, 128.85) * mm, "end": v(-96.5, 126.54) * mm});
            skLineSegment(sketch, "E14.MirrorCS", {"start": v(-126.5, 126.54) * mm, "end": v(-126.5, 121.92) * mm});
            skLineSegment(sketch, "E15.MirrorCS", {"start": v(-32.5, 119.61) * mm, "end": v(-28.5, 121.92) * mm});
            skLineSegment(sketch, "E16.MirrorCS", {"start": v(-2.5, 119.61) * mm, "end": v(1.5, 121.92) * mm});
            skLineSegment(sketch, "E17.MirrorCS", {"start": v(1.5, 126.54) * mm, "end": v(-2.5, 128.85) * mm});
            skLineSegment(sketch, "E18.MirrorCS", {"start": v(57.5, 128.85) * mm, "end": v(53.5, 126.54) * mm});
            skLineSegment(sketch, "E19.MirrorCS", {"start": v(117.5, 119.61) * mm, "end": v(121.5, 121.92) * mm});
            skCircle(sketch, "E20.MirrorC", {"center": v(117.5, 124.23) * mm, "radius": 4 * mm, "construction": true});
            skLineSegment(sketch, "E21.MirrorCS", {"start": v(83.5, 121.92) * mm, "end": v(87.5, 119.61) * mm});
            skLineSegment(sketch, "E22.MirrorCS", {"start": v(-36.5, 121.92) * mm, "end": v(-32.5, 119.61) * mm});
            skLineSegment(sketch, "E23.MirrorCS", {"start": v(-96.5, 126.54) * mm, "end": v(-96.5, 121.92) * mm});
            skLineSegment(sketch, "E24.MirrorCS", {"start": v(23.5, 126.54) * mm, "end": v(23.5, 121.92) * mm});
            skLineSegment(sketch, "E25.MirrorCS", {"start": v(117.5, 128.85) * mm, "end": v(113.5, 126.54) * mm});
            skLineSegment(sketch, "E26.MirrorCS", {"start": v(91.5, 121.92) * mm, "end": v(91.5, 126.54) * mm});
            skCircle(sketch, "E27.MirrorC", {"center": v(27.5, 124.23) * mm, "radius": 4 * mm, "construction": true});
            skLineSegment(sketch, "E28.MirrorCS", {"start": v(-62.5, 119.61) * mm, "end": v(-58.5, 121.92) * mm});
            skCircle(sketch, "E29.MirrorC", {"center": v(57.5, 124.23) * mm, "radius": 4 * mm, "construction": true});
            skLineSegment(sketch, "E30.MirrorCS", {"start": v(91.5, 126.54) * mm, "end": v(87.5, 128.85) * mm});
            skLineSegment(sketch, "E31.MirrorCS", {"start": v(-122.5, 128.85) * mm, "end": v(-126.5, 126.54) * mm});
            skLineSegment(sketch, "E32.MirrorCS", {"start": v(-62.5, 128.85) * mm, "end": v(-66.5, 126.54) * mm});
            skLineSegment(sketch, "E33.MirrorCS", {"start": v(-6.5, 121.92) * mm, "end": v(-2.5, 119.61) * mm});
            skLineSegment(sketch, "E34.MirrorCS", {"start": v(83.5, 126.54) * mm, "end": v(83.5, 121.92) * mm});
            skLineSegment(sketch, "E35.MirrorCS", {"start": v(-32.5, 128.85) * mm, "end": v(-36.5, 126.54) * mm});
            skLineSegment(sketch, "E36.MirrorCS", {"start": v(113.5, 126.54) * mm, "end": v(113.5, 121.92) * mm});
            skLineSegment(sketch, "E37.MirrorCS", {"start": v(-88.5, 121.92) * mm, "end": v(-88.5, 126.54) * mm});
            skLineSegment(sketch, "E38.MirrorCS", {"start": v(23.5, 121.92) * mm, "end": v(27.5, 119.61) * mm});
            skLineSegment(sketch, "E39.MirrorCS", {"start": v(121.5, 126.54) * mm, "end": v(117.5, 128.85) * mm});
            skCircle(sketch, "E40.MirrorC", {"center": v(87.5, 124.23) * mm, "radius": 4 * mm, "construction": true});
            skLineSegment(sketch, "E41.MirrorCS", {"start": v(-118.5, 126.54) * mm, "end": v(-122.5, 128.85) * mm});
            skLineSegment(sketch, "E42.MirrorCS", {"start": v(-58.5, 126.54) * mm, "end": v(-62.5, 128.85) * mm});
            skCircle(sketch, "E43.MirrorC", {"center": v(-122.5, 124.23) * mm, "radius": 4 * mm, "construction": true});
            skLineSegment(sketch, "E44.MirrorCS", {"start": v(53.5, 121.92) * mm, "end": v(57.5, 119.61) * mm});
            skLineSegment(sketch, "E45.MirrorCS", {"start": v(-58.5, 121.92) * mm, "end": v(-58.5, 126.54) * mm});
            skLineSegment(sketch, "E46.MirrorCS", {"start": v(-2.5, 128.85) * mm, "end": v(-6.5, 126.54) * mm});
            skLineSegment(sketch, "E47.MirrorCS", {"start": v(61.5, 121.92) * mm, "end": v(61.5, 126.54) * mm});
            skLineSegment(sketch, "E48.MirrorCS", {"start": v(-28.5, 126.54) * mm, "end": v(-32.5, 128.85) * mm});
            skLineSegment(sketch, "E49.MirrorCS", {"start": v(-88.5, 126.54) * mm, "end": v(-92.5, 128.85) * mm});
            skLineSegment(sketch, "E50.MirrorCS", {"start": v(-66.5, 126.54) * mm, "end": v(-66.5, 121.92) * mm});
            skLineSegment(sketch, "E51.MirrorCS", {"start": v(57.5, 119.61) * mm, "end": v(61.5, 121.92) * mm});
            skLineSegment(sketch, "E52.MirrorCS", {"start": v(121.5, 121.92) * mm, "end": v(121.5, 126.54) * mm});
            skLineSegment(sketch, "E53.MirrorCS", {"start": v(113.5, 121.92) * mm, "end": v(117.5, 119.61) * mm});
            skLineSegment(sketch, "E54.MirrorCS", {"start": v(87.5, 119.61) * mm, "end": v(91.5, 121.92) * mm});
            skLineSegment(sketch, "E55.MirrorCS", {"start": v(31.5, 126.54) * mm, "end": v(27.5, 128.85) * mm});
            skLineSegment(sketch, "E56.MirrorCS", {"start": v(-118.5, 121.92) * mm, "end": v(-118.5, 126.54) * mm});
            skLineSegment(sketch, "E57.MirrorCS", {"start": v(-66.5, 121.92) * mm, "end": v(-62.5, 119.61) * mm});
            skCircle(sketch, "E58.MirrorC", {"center": v(-62.5, 124.23) * mm, "radius": 4 * mm, "construction": true});
            skLineSegment(sketch, "E59.MirrorCS", {"start": v(1.5, 121.92) * mm, "end": v(1.5, 126.54) * mm});
            skLineSegment(sketch, "E60.MirrorCS", {"start": v(-36.5, 126.54) * mm, "end": v(-36.5, 121.92) * mm});
            skLineSegment(sketch, "E61.MirrorCS", {"start": v(-6.5, 126.54) * mm, "end": v(-6.5, 121.92) * mm});
            skLineSegment(sketch, "E62.MirrorCS", {"start": v(-96.5, 121.92) * mm, "end": v(-92.5, 119.61) * mm});
            skLineSegment(sketch, "E63.MirrorCS", {"start": v(61.5, 126.54) * mm, "end": v(57.5, 128.85) * mm});
            skLineSegment(sketch, "E64.MirrorCS", {"start": v(-122.5, 119.61) * mm, "end": v(-118.5, 121.92) * mm});
            skCircle(sketch, "E65.MirrorC", {"center": v(-32.5, 124.23) * mm, "radius": 4 * mm, "construction": true});
            skLineSegment(sketch, "E66.MirrorCS", {"start": v(-28.5, 121.92) * mm, "end": v(-28.5, 126.54) * mm});
            skLineSegment(sketch, "E67.MirrorCS", {"start": v(27.5, 128.85) * mm, "end": v(23.5, 126.54) * mm});
            skCircle(sketch, "E68.MirrorC", {"center": v(-92.5, 124.23) * mm, "radius": 4 * mm, "construction": true});
            skLineSegment(sketch, "E69.MirrorCS", {"start": v(-126.5, 121.92) * mm, "end": v(-122.5, 119.61) * mm});
            skLineSegment(sketch, "E70.MirrorCS", {"start": v(87.5, 128.85) * mm, "end": v(83.5, 126.54) * mm});
            skLineSegment(sketch, "E71.MirrorCS", {"start": v(31.5, 121.92) * mm, "end": v(31.5, 126.54) * mm});
            skCircle(sketch, "E72.MirrorC", {"center": v(-2.5, 124.23) * mm, "radius": 4 * mm, "construction": true});
            skLineSegment(sketch, "E73.MirrorCS", {"start": v(27.5, 119.61) * mm, "end": v(31.5, 121.92) * mm});
            skLineSegment(sketch, "E74.MirrorCS", {"start": v(-92.5, 119.61) * mm, "end": v(-88.5, 121.92) * mm});
            skLineSegment(sketch, "E75.MirrorCS", {"start": v(53.5, 126.54) * mm, "end": v(53.5, 121.92) * mm});
            skPoint(sketch, "E76.MirrorP", {"position": v(119.5, 127.7) * mm});
            skPoint(sketch, "E77.MirrorP", {"position": v(-60.5, 127.7) * mm});
            skPoint(sketch, "E78.MirrorP", {"position": v(-30.5, 127.7) * mm});
            skPoint(sketch, "E79.MirrorP", {"position": v(-120.5, 127.7) * mm});
            skPoint(sketch, "E80.MirrorP", {"position": v(-0.5, 127.7) * mm});
            skPoint(sketch, "E81.MirrorP", {"position": v(-90.5, 127.7) * mm});
            skLineSegment(sketch, "E82.MirrorCS", {"start": v(-126.5, 126.54) * mm, "end": v(-96.5, 126.54) * mm, "construction": true});
            skPoint(sketch, "E83.MirrorP", {"position": v(59.5, 127.7) * mm});
            skPoint(sketch, "E84.MirrorP", {"position": v(89.5, 127.7) * mm});
            skPoint(sketch, "E85.MirrorP", {"position": v(29.5, 127.7) * mm});
            skCircle(sketch, "E86.cCircle", {"center": v(142.5, 104.23) * mm, "radius": 4 * mm, "construction": true});
            skLineSegment(sketch, "E86.0", {"start": v(146.5, 101.92) * mm, "end": v(142.5, 99.61) * mm});
            skLineSegment(sketch, "E86.1", {"start": v(142.5, 99.61) * mm, "end": v(138.5, 101.92) * mm});
            skLineSegment(sketch, "E86.2", {"start": v(138.5, 101.92) * mm, "end": v(138.5, 106.54) * mm});
            skLineSegment(sketch, "E86.3", {"start": v(138.5, 106.54) * mm, "end": v(142.5, 108.85) * mm});
            skLineSegment(sketch, "E86.4", {"start": v(142.5, 108.85) * mm, "end": v(146.5, 106.54) * mm});
            skLineSegment(sketch, "E86.5", {"start": v(146.5, 106.54) * mm, "end": v(146.5, 101.92) * mm});
            skPoint(sketch, "E86.0.midPoint", {"position": v(144.5, 100.77) * mm});
            skLineSegment(sketch, "E87.0.1.0", {"start": v(142.5, 78.85) * mm, "end": v(146.5, 76.54) * mm});
            skLineSegment(sketch, "E87.0.1.1", {"start": v(138.5, 76.54) * mm, "end": v(142.5, 78.85) * mm});
            skLineSegment(sketch, "E87.0.1.2", {"start": v(138.5, 71.92) * mm, "end": v(138.5, 76.54) * mm});
            skPoint(sketch, "E87.0.1.3", {"position": v(144.5, 70.77) * mm});
            skCircle(sketch, "E87.0.1.4", {"center": v(142.5, 74.23) * mm, "radius": 4 * mm, "construction": true});
            skLineSegment(sketch, "E87.0.1.5", {"start": v(146.5, 76.54) * mm, "end": v(146.5, 71.92) * mm});
            skLineSegment(sketch, "E87.0.1.6", {"start": v(142.5, 69.61) * mm, "end": v(138.5, 71.92) * mm});
            skLineSegment(sketch, "E87.0.1.7", {"start": v(146.5, 71.92) * mm, "end": v(142.5, 69.61) * mm});
            skLineSegment(sketch, "E87.0.2.0", {"start": v(142.5, 48.85) * mm, "end": v(146.5, 46.54) * mm});
            skLineSegment(sketch, "E87.0.2.1", {"start": v(138.5, 46.54) * mm, "end": v(142.5, 48.85) * mm});
            skLineSegment(sketch, "E87.0.2.2", {"start": v(138.5, 41.92) * mm, "end": v(138.5, 46.54) * mm});
            skPoint(sketch, "E87.0.2.3", {"position": v(144.5, 40.77) * mm});
            skCircle(sketch, "E87.0.2.4", {"center": v(142.5, 44.23) * mm, "radius": 4 * mm, "construction": true});
            skLineSegment(sketch, "E87.0.2.5", {"start": v(146.5, 46.54) * mm, "end": v(146.5, 41.92) * mm});
            skLineSegment(sketch, "E87.0.2.6", {"start": v(142.5, 39.61) * mm, "end": v(138.5, 41.92) * mm});
            skLineSegment(sketch, "E87.0.2.7", {"start": v(146.5, 41.92) * mm, "end": v(142.5, 39.61) * mm});
            skLineSegment(sketch, "E87.0.3.0", {"start": v(142.5, 18.85) * mm, "end": v(146.5, 16.54) * mm});
            skLineSegment(sketch, "E87.0.3.1", {"start": v(138.5, 16.54) * mm, "end": v(142.5, 18.85) * mm});
            skLineSegment(sketch, "E87.0.3.2", {"start": v(138.5, 11.92) * mm, "end": v(138.5, 16.54) * mm});
            skPoint(sketch, "E87.0.3.3", {"position": v(144.5, 10.77) * mm});
            skCircle(sketch, "E87.0.3.4", {"center": v(142.5, 14.23) * mm, "radius": 4 * mm, "construction": true});
            skLineSegment(sketch, "E87.0.3.5", {"start": v(146.5, 16.54) * mm, "end": v(146.5, 11.92) * mm});
            skLineSegment(sketch, "E87.0.3.6", {"start": v(142.5, 9.61) * mm, "end": v(138.5, 11.92) * mm});
            skLineSegment(sketch, "E87.0.3.7", {"start": v(146.5, 11.92) * mm, "end": v(142.5, 9.61) * mm});
            skLineSegment(sketch, "E87.0.4.0", {"start": v(142.5, -11.15) * mm, "end": v(146.5, -13.46) * mm});
            skLineSegment(sketch, "E87.0.4.1", {"start": v(138.5, -13.46) * mm, "end": v(142.5, -11.15) * mm});
            skLineSegment(sketch, "E87.0.4.2", {"start": v(138.5, -18.08) * mm, "end": v(138.5, -13.46) * mm});
            skPoint(sketch, "E87.0.4.3", {"position": v(144.5, -19.23) * mm});
            skCircle(sketch, "E87.0.4.4", {"center": v(142.5, -15.77) * mm, "radius": 4 * mm, "construction": true});
            skLineSegment(sketch, "E87.0.4.5", {"start": v(146.5, -13.46) * mm, "end": v(146.5, -18.08) * mm});
            skLineSegment(sketch, "E87.0.4.6", {"start": v(142.5, -20.39) * mm, "end": v(138.5, -18.08) * mm});
            skLineSegment(sketch, "E87.0.4.7", {"start": v(146.5, -18.08) * mm, "end": v(142.5, -20.39) * mm});
            skLineSegment(sketch, "E87.0.5.0", {"start": v(142.5, -41.15) * mm, "end": v(146.5, -43.46) * mm});
            skLineSegment(sketch, "E87.0.5.1", {"start": v(138.5, -43.46) * mm, "end": v(142.5, -41.15) * mm});
            skLineSegment(sketch, "E87.0.5.2", {"start": v(138.5, -48.08) * mm, "end": v(138.5, -43.46) * mm});
            skPoint(sketch, "E87.0.5.3", {"position": v(144.5, -49.23) * mm});
            skCircle(sketch, "E87.0.5.4", {"center": v(142.5, -45.77) * mm, "radius": 4 * mm, "construction": true});
            skLineSegment(sketch, "E87.0.5.5", {"start": v(146.5, -43.46) * mm, "end": v(146.5, -48.08) * mm});
            skLineSegment(sketch, "E87.0.5.6", {"start": v(142.5, -50.39) * mm, "end": v(138.5, -48.08) * mm});
            skLineSegment(sketch, "E87.0.5.7", {"start": v(146.5, -48.08) * mm, "end": v(142.5, -50.39) * mm});
            skLineSegment(sketch, "E87.0.6.0", {"start": v(142.5, -71.15) * mm, "end": v(146.5, -73.46) * mm});
            skLineSegment(sketch, "E87.0.6.1", {"start": v(138.5, -73.46) * mm, "end": v(142.5, -71.15) * mm});
            skLineSegment(sketch, "E87.0.6.2", {"start": v(138.5, -78.08) * mm, "end": v(138.5, -73.46) * mm});
            skPoint(sketch, "E87.0.6.3", {"position": v(144.5, -79.23) * mm});
            skCircle(sketch, "E87.0.6.4", {"center": v(142.5, -75.77) * mm, "radius": 4 * mm, "construction": true});
            skLineSegment(sketch, "E87.0.6.5", {"start": v(146.5, -73.46) * mm, "end": v(146.5, -78.08) * mm});
            skLineSegment(sketch, "E87.0.6.6", {"start": v(142.5, -80.39) * mm, "end": v(138.5, -78.08) * mm});
            skLineSegment(sketch, "E87.0.6.7", {"start": v(146.5, -78.08) * mm, "end": v(142.5, -80.39) * mm});
            skLineSegment(sketch, "E87.0.7.0", {"start": v(142.5, -101.15) * mm, "end": v(146.5, -103.46) * mm});
            skLineSegment(sketch, "E87.0.7.1", {"start": v(138.5, -103.46) * mm, "end": v(142.5, -101.15) * mm});
            skLineSegment(sketch, "E87.0.7.2", {"start": v(138.5, -108.08) * mm, "end": v(138.5, -103.46) * mm});
            skPoint(sketch, "E87.0.7.3", {"position": v(144.5, -109.23) * mm});
            skCircle(sketch, "E87.0.7.4", {"center": v(142.5, -105.77) * mm, "radius": 4 * mm, "construction": true});
            skLineSegment(sketch, "E87.0.7.5", {"start": v(146.5, -103.46) * mm, "end": v(146.5, -108.08) * mm});
            skLineSegment(sketch, "E87.0.7.6", {"start": v(142.5, -110.39) * mm, "end": v(138.5, -108.08) * mm});
            skLineSegment(sketch, "E87.0.7.7", {"start": v(146.5, -108.08) * mm, "end": v(142.5, -110.39) * mm});
            skLineSegment(sketch, "E87.0.8.0", {"start": v(142.5, -131.15) * mm, "end": v(146.5, -133.46) * mm});
            skLineSegment(sketch, "E87.0.8.1", {"start": v(138.5, -133.46) * mm, "end": v(142.5, -131.15) * mm});
            skLineSegment(sketch, "E87.0.8.2", {"start": v(138.5, -138.08) * mm, "end": v(138.5, -133.46) * mm});
            skPoint(sketch, "E87.0.8.3", {"position": v(144.5, -139.23) * mm});
            skCircle(sketch, "E87.0.8.4", {"center": v(142.5, -135.77) * mm, "radius": 4 * mm, "construction": true});
            skLineSegment(sketch, "E87.0.8.5", {"start": v(146.5, -133.46) * mm, "end": v(146.5, -138.08) * mm});
            skLineSegment(sketch, "E87.0.8.6", {"start": v(142.5, -140.39) * mm, "end": v(138.5, -138.08) * mm});
            skLineSegment(sketch, "E87.0.8.7", {"start": v(146.5, -138.08) * mm, "end": v(142.5, -140.39) * mm});
            skLineSegment(sketch, "E87.direction1", {"start": v(138.5, 101.92) * mm, "end": v(161, 101.92) * mm, "construction": true});
            skLineSegment(sketch, "E87.direction2", {"start": v(138.5, 101.92) * mm, "end": v(138.5, 71.92) * mm, "construction": true});
            skLineSegment(sketch, "E88.MirrorCS", {"start": v(-142.5, 99.61) * mm, "end": v(-138.5, 101.92) * mm});
            skLineSegment(sketch, "E89.MirrorCS", {"start": v(-146.5, -18.08) * mm, "end": v(-142.5, -20.39) * mm});
            skLineSegment(sketch, "E90.MirrorCS", {"start": v(-142.5, -20.39) * mm, "end": v(-138.5, -18.08) * mm});
            skLineSegment(sketch, "E91.MirrorCS", {"start": v(-142.5, -11.15) * mm, "end": v(-146.5, -13.46) * mm});
            skLineSegment(sketch, "E92.MirrorCS", {"start": v(-138.5, 101.92) * mm, "end": v(-138.5, 106.54) * mm});
            skLineSegment(sketch, "E93.MirrorCS", {"start": v(-138.5, -18.08) * mm, "end": v(-138.5, -13.46) * mm});
            skLineSegment(sketch, "E94.MirrorCS", {"start": v(-146.5, 16.54) * mm, "end": v(-146.5, 11.92) * mm});
            skLineSegment(sketch, "E95.MirrorCS", {"start": v(-146.5, -48.08) * mm, "end": v(-142.5, -50.39) * mm});
            skLineSegment(sketch, "E96.MirrorCS", {"start": v(-138.5, 71.92) * mm, "end": v(-138.5, 76.54) * mm});
            skLineSegment(sketch, "E97.MirrorCS", {"start": v(-142.5, -71.15) * mm, "end": v(-146.5, -73.46) * mm});
            skLineSegment(sketch, "E98.MirrorCS", {"start": v(-138.5, 76.54) * mm, "end": v(-142.5, 78.85) * mm});
            skLineSegment(sketch, "E99.MirrorCS", {"start": v(-142.5, -50.39) * mm, "end": v(-138.5, -48.08) * mm});
            skLineSegment(sketch, "E100.MirrorCS", {"start": v(-142.5, 69.61) * mm, "end": v(-138.5, 71.92) * mm});
            skCircle(sketch, "E101.MirrorC", {"center": v(-142.5, -15.77) * mm, "radius": 4 * mm, "construction": true});
            skLineSegment(sketch, "E102.MirrorCS", {"start": v(-142.5, -80.39) * mm, "end": v(-138.5, -78.08) * mm});
            skLineSegment(sketch, "E103.MirrorCS", {"start": v(-146.5, 11.92) * mm, "end": v(-142.5, 9.61) * mm});
            skLineSegment(sketch, "E104.MirrorCS", {"start": v(-146.5, 76.54) * mm, "end": v(-146.5, 71.92) * mm});
            skLineSegment(sketch, "E105.MirrorCS", {"start": v(-146.5, 46.54) * mm, "end": v(-146.5, 41.92) * mm});
            skLineSegment(sketch, "E106.MirrorCS", {"start": v(-138.5, -13.46) * mm, "end": v(-142.5, -11.15) * mm});
            skLineSegment(sketch, "E107.MirrorCS", {"start": v(-146.5, 71.92) * mm, "end": v(-142.5, 69.61) * mm});
            skLineSegment(sketch, "E108.MirrorCS", {"start": v(-142.5, -140.39) * mm, "end": v(-138.5, -138.08) * mm});
            skLineSegment(sketch, "E109.MirrorCS", {"start": v(-142.5, -41.15) * mm, "end": v(-146.5, -43.46) * mm});
            skLineSegment(sketch, "E110.MirrorCS", {"start": v(-142.5, 39.61) * mm, "end": v(-138.5, 41.92) * mm});
            skLineSegment(sketch, "E111.MirrorCS", {"start": v(-142.5, 9.61) * mm, "end": v(-138.5, 11.92) * mm});
            skLineSegment(sketch, "E112.MirrorCS", {"start": v(-146.5, -133.46) * mm, "end": v(-146.5, -138.08) * mm});
            skLineSegment(sketch, "E113.MirrorCS", {"start": v(-146.5, 41.92) * mm, "end": v(-142.5, 39.61) * mm});
            skLineSegment(sketch, "E114.MirrorCS", {"start": v(-138.5, 41.92) * mm, "end": v(-138.5, 46.54) * mm});
            skLineSegment(sketch, "E115.MirrorCS", {"start": v(-146.5, -73.46) * mm, "end": v(-146.5, -78.08) * mm});
            skLineSegment(sketch, "E116.MirrorCS", {"start": v(-146.5, -78.08) * mm, "end": v(-142.5, -80.39) * mm});
            skLineSegment(sketch, "E117.MirrorCS", {"start": v(-146.5, -13.46) * mm, "end": v(-146.5, -18.08) * mm});
            skLineSegment(sketch, "E118.MirrorCS", {"start": v(-138.5, -48.08) * mm, "end": v(-138.5, -43.46) * mm});
            skLineSegment(sketch, "E119.MirrorCS", {"start": v(-146.5, -138.08) * mm, "end": v(-142.5, -140.39) * mm});
            skLineSegment(sketch, "E120.MirrorCS", {"start": v(-138.5, 11.92) * mm, "end": v(-138.5, 16.54) * mm});
            skLineSegment(sketch, "E121.MirrorCS", {"start": v(-138.5, -138.08) * mm, "end": v(-138.5, -133.46) * mm});
            skLineSegment(sketch, "E122.MirrorCS", {"start": v(-142.5, -110.39) * mm, "end": v(-138.5, -108.08) * mm});
            skLineSegment(sketch, "E123.MirrorCS", {"start": v(-146.5, -108.08) * mm, "end": v(-142.5, -110.39) * mm});
            skLineSegment(sketch, "E124.MirrorCS", {"start": v(-138.5, -73.46) * mm, "end": v(-142.5, -71.15) * mm});
            skLineSegment(sketch, "E125.MirrorCS", {"start": v(-138.5, -78.08) * mm, "end": v(-138.5, -73.46) * mm});
            skLineSegment(sketch, "E126.MirrorCS", {"start": v(-146.5, 106.54) * mm, "end": v(-146.5, 101.92) * mm});
            skLineSegment(sketch, "E127.MirrorCS", {"start": v(-146.5, -43.46) * mm, "end": v(-146.5, -48.08) * mm});
            skLineSegment(sketch, "E128.MirrorCS", {"start": v(-146.5, 101.92) * mm, "end": v(-142.5, 99.61) * mm});
            skLineSegment(sketch, "E129.MirrorCS", {"start": v(-138.5, -133.46) * mm, "end": v(-142.5, -131.15) * mm});
            skLineSegment(sketch, "E130.MirrorCS", {"start": v(-142.5, -131.15) * mm, "end": v(-146.5, -133.46) * mm});
            skCircle(sketch, "E131.MirrorC", {"center": v(-142.5, 44.23) * mm, "radius": 4 * mm, "construction": true});
            skLineSegment(sketch, "E132.MirrorCS", {"start": v(-138.5, 46.54) * mm, "end": v(-142.5, 48.85) * mm});
            skLineSegment(sketch, "E133.MirrorCS", {"start": v(-138.5, -103.46) * mm, "end": v(-142.5, -101.15) * mm});
            skCircle(sketch, "E134.MirrorC", {"center": v(-142.5, 104.23) * mm, "radius": 4 * mm, "construction": true});
            skCircle(sketch, "E135.MirrorC", {"center": v(-142.5, -75.77) * mm, "radius": 4 * mm, "construction": true});
            skLineSegment(sketch, "E136.MirrorCS", {"start": v(-138.5, -108.08) * mm, "end": v(-138.5, -103.46) * mm});
            skCircle(sketch, "E137.MirrorC", {"center": v(-142.5, 74.23) * mm, "radius": 4 * mm, "construction": true});
            skLineSegment(sketch, "E138.MirrorCS", {"start": v(-138.5, 106.54) * mm, "end": v(-142.5, 108.85) * mm});
            skCircle(sketch, "E139.MirrorC", {"center": v(-142.5, -105.77) * mm, "radius": 4 * mm, "construction": true});
            skLineSegment(sketch, "E140.MirrorCS", {"start": v(-138.5, -43.46) * mm, "end": v(-142.5, -41.15) * mm});
            skLineSegment(sketch, "E141.MirrorCS", {"start": v(-142.5, 48.85) * mm, "end": v(-146.5, 46.54) * mm});
            skLineSegment(sketch, "E142.MirrorCS", {"start": v(-142.5, 18.85) * mm, "end": v(-146.5, 16.54) * mm});
            skLineSegment(sketch, "E143.MirrorCS", {"start": v(-146.5, -103.46) * mm, "end": v(-146.5, -108.08) * mm});
            skLineSegment(sketch, "E144.MirrorCS", {"start": v(-142.5, 108.85) * mm, "end": v(-146.5, 106.54) * mm});
            skCircle(sketch, "E145.MirrorC", {"center": v(-142.5, 14.23) * mm, "radius": 4 * mm, "construction": true});
            skCircle(sketch, "E146.MirrorC", {"center": v(-142.5, -45.77) * mm, "radius": 4 * mm, "construction": true});
            skLineSegment(sketch, "E147.MirrorCS", {"start": v(-142.5, 78.85) * mm, "end": v(-146.5, 76.54) * mm});
            skLineSegment(sketch, "E148.MirrorCS", {"start": v(-138.5, 16.54) * mm, "end": v(-142.5, 18.85) * mm});
            skLineSegment(sketch, "E149.MirrorCS", {"start": v(-142.5, -101.15) * mm, "end": v(-146.5, -103.46) * mm});
            skCircle(sketch, "E150.MirrorC", {"center": v(-142.5, -135.77) * mm, "radius": 4 * mm, "construction": true});
            skPoint(sketch, "E151.MirrorP", {"position": v(-144.5, 40.77) * mm});
            skLineSegment(sketch, "E152.MirrorCS", {"start": v(-138.5, 101.92) * mm, "end": v(-138.5, 71.92) * mm, "construction": true});
            skPoint(sketch, "E153.MirrorP", {"position": v(-144.5, 100.77) * mm});
            skPoint(sketch, "E154.MirrorP", {"position": v(-144.5, -19.23) * mm});
            skPoint(sketch, "E155.MirrorP", {"position": v(-144.5, -49.23) * mm});
            skPoint(sketch, "E156.MirrorP", {"position": v(-144.5, 10.77) * mm});
            skPoint(sketch, "E157.MirrorP", {"position": v(-144.5, 70.77) * mm});
            skPoint(sketch, "E158.MirrorP", {"position": v(-144.5, -139.23) * mm});
            skPoint(sketch, "E159.MirrorP", {"position": v(-144.5, -109.23) * mm});
            skPoint(sketch, "E160.MirrorP", {"position": v(-144.5, -79.23) * mm});
            skSolve(sketch);
        }
        {
            var Q0;
            Q0=makeQuery(id+"F0.imprint","IMPRINT",FACE,{"disambiguationData":[TD([[makeQuery(id+"F0.imprint","IMPRINT",EDGE,{"derivedFrom":sQuery(id+"F0.wireOp",EDGE,"E0.bottom")}),-1.0]])]});
            extrude(context, id + "F1", {"entities" : qUnion([Q0]), "depth" : 5 * mm, "offsetDistance" : 25 * mm});
        }
        {
            var Q0;
            Q0=qCreatedBy(makeId("Front.planeOp"),FACE);
            var sketch = newSketch(context, id + "F2", { "sketchPlane" : qUnion([Q0])});
            skLineSegment(sketch, "E161.bottom", {"start": v(-505, 134.17) * mm, "end": v(-200, 134.17) * mm});
            skLineSegment(sketch, "E161.top", {"start": v(-505, -170.83) * mm, "end": v(-200, -170.83) * mm});
            skLineSegment(sketch, "E161.left", {"start": v(-505, 134.17) * mm, "end": v(-505, -170.83) * mm});
            skLineSegment(sketch, "E161.right", {"start": v(-200, 134.17) * mm, "end": v(-200, -170.83) * mm});
            skCircle(sketch, "E162", {"center": v(-495, 124.17) * mm, "radius": 2.5 * mm});
            skLineSegment(sketch, "E163", {"start": v(-352.5, 134.17) * mm, "end": v(-352.5, -170.83) * mm, "construction": true});
            skLineSegment(sketch, "E164", {"start": v(-505, -18.33) * mm, "end": v(-200, -18.33) * mm, "construction": true});
            skLineSegment(sketch, "E165.MirrorCS", {"start": v(-200, -18.33) * mm, "end": v(-505, -18.33) * mm, "construction": true});
            skCircle(sketch, "E166.MirrorC", {"center": v(-210, 124.17) * mm, "radius": 2.5 * mm});
            skCircle(sketch, "E167.MirrorC", {"center": v(-495, -160.83) * mm, "radius": 2.5 * mm});
            skCircle(sketch, "E168.MirrorC", {"center": v(-210, -160.83) * mm, "radius": 2.5 * mm});
            skCircle(sketch, "E169", {"center": v(-210, 104.17) * mm, "radius": 2.5 * mm});
            skCircle(sketch, "E170", {"center": v(-475, -160.83) * mm, "radius": 2.5 * mm});
            skCircle(sketch, "E171", {"center": v(-475, 104.17) * mm, "radius": 2.5 * mm});
            skCircle(sketch, "E172.0.1.0", {"center": v(-210, 74.17) * mm, "radius": 2.5 * mm});
            skCircle(sketch, "E172.0.2.0", {"center": v(-210, 44.17) * mm, "radius": 2.5 * mm});
            skCircle(sketch, "E172.0.3.0", {"center": v(-210, 14.17) * mm, "radius": 2.5 * mm});
            skCircle(sketch, "E172.0.4.0", {"center": v(-210, -15.83) * mm, "radius": 2.5 * mm});
            skCircle(sketch, "E172.0.5.0", {"center": v(-210, -45.83) * mm, "radius": 2.5 * mm});
            skCircle(sketch, "E172.0.6.0", {"center": v(-210, -75.83) * mm, "radius": 2.5 * mm});
            skCircle(sketch, "E172.0.7.0", {"center": v(-210, -105.83) * mm, "radius": 2.5 * mm});
            skCircle(sketch, "E172.0.8.0", {"center": v(-210, -135.83) * mm, "radius": 2.5 * mm});
            skLineSegment(sketch, "E172.direction1", {"start": v(-210, 104.17) * mm, "end": v(-185, 104.17) * mm, "construction": true});
            skLineSegment(sketch, "E172.direction2", {"start": v(-210, 104.17) * mm, "end": v(-210, 74.17) * mm, "construction": true});
            skCircle(sketch, "E173.1.0.0", {"center": v(-445, -160.83) * mm, "radius": 2.5 * mm});
            skCircle(sketch, "E173.2.0.0", {"center": v(-415, -160.83) * mm, "radius": 2.5 * mm});
            skCircle(sketch, "E173.3.0.0", {"center": v(-385, -160.83) * mm, "radius": 2.5 * mm});
            skCircle(sketch, "E173.4.0.0", {"center": v(-355, -160.83) * mm, "radius": 2.5 * mm});
            skCircle(sketch, "E173.5.0.0", {"center": v(-325, -160.83) * mm, "radius": 2.5 * mm});
            skCircle(sketch, "E173.6.0.0", {"center": v(-295, -160.83) * mm, "radius": 2.5 * mm});
            skCircle(sketch, "E173.7.0.0", {"center": v(-265, -160.83) * mm, "radius": 2.5 * mm});
            skCircle(sketch, "E173.8.0.0", {"center": v(-235, -160.83) * mm, "radius": 2.5 * mm});
            skLineSegment(sketch, "E173.direction1", {"start": v(-475, -160.83) * mm, "end": v(-445, -160.83) * mm, "construction": true});
            skCircle(sketch, "E174.MirrorC", {"center": v(-495, 104.17) * mm, "radius": 2.5 * mm});
            skCircle(sketch, "E175.MirrorC", {"center": v(-495, 74.17) * mm, "radius": 2.5 * mm});
            skCircle(sketch, "E176.MirrorC", {"center": v(-495, -75.83) * mm, "radius": 2.5 * mm});
            skCircle(sketch, "E177.MirrorC", {"center": v(-495, -15.83) * mm, "radius": 2.5 * mm});
            skCircle(sketch, "E178.MirrorC", {"center": v(-495, -135.83) * mm, "radius": 2.5 * mm});
            skCircle(sketch, "E179.MirrorC", {"center": v(-495, -105.83) * mm, "radius": 2.5 * mm});
            skCircle(sketch, "E180.MirrorC", {"center": v(-495, -45.83) * mm, "radius": 2.5 * mm});
            skCircle(sketch, "E181.MirrorC", {"center": v(-495, 14.17) * mm, "radius": 2.5 * mm});
            skCircle(sketch, "E182.MirrorC", {"center": v(-495, 44.17) * mm, "radius": 2.5 * mm});
            skLineSegment(sketch, "E183.MirrorCS", {"start": v(-495, 104.17) * mm, "end": v(-495, 74.17) * mm, "construction": true});
            skCircle(sketch, "E184.MirrorC", {"center": v(-475, 124.17) * mm, "radius": 2.5 * mm});
            skCircle(sketch, "E185.MirrorC", {"center": v(-445, 124.17) * mm, "radius": 2.5 * mm});
            skCircle(sketch, "E186.MirrorC", {"center": v(-265, 124.17) * mm, "radius": 2.5 * mm});
            skCircle(sketch, "E187.MirrorC", {"center": v(-415, 124.17) * mm, "radius": 2.5 * mm});
            skCircle(sketch, "E188.MirrorC", {"center": v(-235, 124.17) * mm, "radius": 2.5 * mm});
            skCircle(sketch, "E189.MirrorC", {"center": v(-295, 124.17) * mm, "radius": 2.5 * mm});
            skCircle(sketch, "E190.MirrorC", {"center": v(-325, 124.17) * mm, "radius": 2.5 * mm});
            skCircle(sketch, "E191.MirrorC", {"center": v(-355, 124.17) * mm, "radius": 2.5 * mm});
            skCircle(sketch, "E192.MirrorC", {"center": v(-385, 124.17) * mm, "radius": 2.5 * mm});
            skLineSegment(sketch, "E193.MirrorCS", {"start": v(-475, 124.17) * mm, "end": v(-445, 124.17) * mm, "construction": true});
            skCircle(sketch, "E194.0.1.0", {"center": v(-475, 74.17) * mm, "radius": 2.5 * mm});
            skCircle(sketch, "E194.0.2.0", {"center": v(-475, 44.17) * mm, "radius": 2.5 * mm});
            skCircle(sketch, "E194.0.3.0", {"center": v(-475, 14.17) * mm, "radius": 2.5 * mm});
            skCircle(sketch, "E194.0.4.0", {"center": v(-475, -15.83) * mm, "radius": 2.5 * mm});
            skCircle(sketch, "E194.0.5.0", {"center": v(-475, -45.83) * mm, "radius": 2.5 * mm});
            skCircle(sketch, "E194.0.6.0", {"center": v(-475, -75.83) * mm, "radius": 2.5 * mm});
            skCircle(sketch, "E194.0.7.0", {"center": v(-475, -105.83) * mm, "radius": 2.5 * mm});
            skCircle(sketch, "E194.0.8.0", {"center": v(-475, -135.83) * mm, "radius": 2.5 * mm});
            skCircle(sketch, "E194.1.0.0", {"center": v(-445, 104.17) * mm, "radius": 2.5 * mm});
            skCircle(sketch, "E194.1.1.0", {"center": v(-445, 74.17) * mm, "radius": 2.5 * mm});
            skCircle(sketch, "E194.1.2.0", {"center": v(-445, 44.17) * mm, "radius": 2.5 * mm});
            skCircle(sketch, "E194.1.3.0", {"center": v(-445, 14.17) * mm, "radius": 2.5 * mm});
            skCircle(sketch, "E194.1.4.0", {"center": v(-445, -15.83) * mm, "radius": 2.5 * mm});
            skCircle(sketch, "E194.1.5.0", {"center": v(-445, -45.83) * mm, "radius": 2.5 * mm});
            skCircle(sketch, "E194.1.6.0", {"center": v(-445, -75.83) * mm, "radius": 2.5 * mm});
            skCircle(sketch, "E194.1.7.0", {"center": v(-445, -105.83) * mm, "radius": 2.5 * mm});
            skCircle(sketch, "E194.1.8.0", {"center": v(-445, -135.83) * mm, "radius": 2.5 * mm});
            skCircle(sketch, "E194.2.0.0", {"center": v(-415, 104.17) * mm, "radius": 2.5 * mm});
            skCircle(sketch, "E194.2.1.0", {"center": v(-415, 74.17) * mm, "radius": 2.5 * mm});
            skCircle(sketch, "E194.2.2.0", {"center": v(-415, 44.17) * mm, "radius": 2.5 * mm});
            skCircle(sketch, "E194.2.3.0", {"center": v(-415, 14.17) * mm, "radius": 2.5 * mm});
            skCircle(sketch, "E194.2.4.0", {"center": v(-415, -15.83) * mm, "radius": 2.5 * mm});
            skCircle(sketch, "E194.2.5.0", {"center": v(-415, -45.83) * mm, "radius": 2.5 * mm});
            skCircle(sketch, "E194.2.6.0", {"center": v(-415, -75.83) * mm, "radius": 2.5 * mm});
            skCircle(sketch, "E194.2.7.0", {"center": v(-415, -105.83) * mm, "radius": 2.5 * mm});
            skCircle(sketch, "E194.2.8.0", {"center": v(-415, -135.83) * mm, "radius": 2.5 * mm});
            skCircle(sketch, "E194.3.0.0", {"center": v(-385, 104.17) * mm, "radius": 2.5 * mm});
            skCircle(sketch, "E194.3.1.0", {"center": v(-385, 74.17) * mm, "radius": 2.5 * mm});
            skCircle(sketch, "E194.3.2.0", {"center": v(-385, 44.17) * mm, "radius": 2.5 * mm});
            skCircle(sketch, "E194.3.3.0", {"center": v(-385, 14.17) * mm, "radius": 2.5 * mm});
            skCircle(sketch, "E194.3.4.0", {"center": v(-385, -15.83) * mm, "radius": 2.5 * mm});
            skCircle(sketch, "E194.3.5.0", {"center": v(-385, -45.83) * mm, "radius": 2.5 * mm});
            skCircle(sketch, "E194.3.6.0", {"center": v(-385, -75.83) * mm, "radius": 2.5 * mm});
            skCircle(sketch, "E194.3.7.0", {"center": v(-385, -105.83) * mm, "radius": 2.5 * mm});
            skCircle(sketch, "E194.3.8.0", {"center": v(-385, -135.83) * mm, "radius": 2.5 * mm});
            skCircle(sketch, "E194.4.0.0", {"center": v(-355, 104.17) * mm, "radius": 2.5 * mm});
            skCircle(sketch, "E194.4.1.0", {"center": v(-355, 74.17) * mm, "radius": 2.5 * mm});
            skCircle(sketch, "E194.4.2.0", {"center": v(-355, 44.17) * mm, "radius": 2.5 * mm});
            skCircle(sketch, "E194.4.3.0", {"center": v(-355, 14.17) * mm, "radius": 2.5 * mm});
            skCircle(sketch, "E194.4.4.0", {"center": v(-355, -15.83) * mm, "radius": 2.5 * mm});
            skCircle(sketch, "E194.4.5.0", {"center": v(-355, -45.83) * mm, "radius": 2.5 * mm});
            skCircle(sketch, "E194.4.6.0", {"center": v(-355, -75.83) * mm, "radius": 2.5 * mm});
            skCircle(sketch, "E194.4.7.0", {"center": v(-355, -105.83) * mm, "radius": 2.5 * mm});
            skCircle(sketch, "E194.4.8.0", {"center": v(-355, -135.83) * mm, "radius": 2.5 * mm});
            skCircle(sketch, "E194.5.0.0", {"center": v(-325, 104.17) * mm, "radius": 2.5 * mm});
            skCircle(sketch, "E194.5.1.0", {"center": v(-325, 74.17) * mm, "radius": 2.5 * mm});
            skCircle(sketch, "E194.5.2.0", {"center": v(-325, 44.17) * mm, "radius": 2.5 * mm});
            skCircle(sketch, "E194.5.3.0", {"center": v(-325, 14.17) * mm, "radius": 2.5 * mm});
            skCircle(sketch, "E194.5.4.0", {"center": v(-325, -15.83) * mm, "radius": 2.5 * mm});
            skCircle(sketch, "E194.5.5.0", {"center": v(-325, -45.83) * mm, "radius": 2.5 * mm});
            skCircle(sketch, "E194.5.6.0", {"center": v(-325, -75.83) * mm, "radius": 2.5 * mm});
            skCircle(sketch, "E194.5.7.0", {"center": v(-325, -105.83) * mm, "radius": 2.5 * mm});
            skCircle(sketch, "E194.5.8.0", {"center": v(-325, -135.83) * mm, "radius": 2.5 * mm});
            skCircle(sketch, "E194.6.0.0", {"center": v(-295, 104.17) * mm, "radius": 2.5 * mm});
            skCircle(sketch, "E194.6.1.0", {"center": v(-295, 74.17) * mm, "radius": 2.5 * mm});
            skCircle(sketch, "E194.6.2.0", {"center": v(-295, 44.17) * mm, "radius": 2.5 * mm});
            skCircle(sketch, "E194.6.3.0", {"center": v(-295, 14.17) * mm, "radius": 2.5 * mm});
            skCircle(sketch, "E194.6.4.0", {"center": v(-295, -15.83) * mm, "radius": 2.5 * mm});
            skCircle(sketch, "E194.6.5.0", {"center": v(-295, -45.83) * mm, "radius": 2.5 * mm});
            skCircle(sketch, "E194.6.6.0", {"center": v(-295, -75.83) * mm, "radius": 2.5 * mm});
            skCircle(sketch, "E194.6.7.0", {"center": v(-295, -105.83) * mm, "radius": 2.5 * mm});
            skCircle(sketch, "E194.6.8.0", {"center": v(-295, -135.83) * mm, "radius": 2.5 * mm});
            skCircle(sketch, "E194.7.0.0", {"center": v(-265, 104.17) * mm, "radius": 2.5 * mm});
            skCircle(sketch, "E194.7.1.0", {"center": v(-265, 74.17) * mm, "radius": 2.5 * mm});
            skCircle(sketch, "E194.7.2.0", {"center": v(-265, 44.17) * mm, "radius": 2.5 * mm});
            skCircle(sketch, "E194.7.3.0", {"center": v(-265, 14.17) * mm, "radius": 2.5 * mm});
            skCircle(sketch, "E194.7.4.0", {"center": v(-265, -15.83) * mm, "radius": 2.5 * mm});
            skCircle(sketch, "E194.7.5.0", {"center": v(-265, -45.83) * mm, "radius": 2.5 * mm});
            skCircle(sketch, "E194.7.6.0", {"center": v(-265, -75.83) * mm, "radius": 2.5 * mm});
            skCircle(sketch, "E194.7.7.0", {"center": v(-265, -105.83) * mm, "radius": 2.5 * mm});
            skCircle(sketch, "E194.7.8.0", {"center": v(-265, -135.83) * mm, "radius": 2.5 * mm});
            skCircle(sketch, "E194.8.0.0", {"center": v(-235, 104.17) * mm, "radius": 2.5 * mm});
            skCircle(sketch, "E194.8.1.0", {"center": v(-235, 74.17) * mm, "radius": 2.5 * mm});
            skCircle(sketch, "E194.8.2.0", {"center": v(-235, 44.17) * mm, "radius": 2.5 * mm});
            skCircle(sketch, "E194.8.3.0", {"center": v(-235, 14.17) * mm, "radius": 2.5 * mm});
            skCircle(sketch, "E194.8.4.0", {"center": v(-235, -15.83) * mm, "radius": 2.5 * mm});
            skCircle(sketch, "E194.8.5.0", {"center": v(-235, -45.83) * mm, "radius": 2.5 * mm});
            skCircle(sketch, "E194.8.6.0", {"center": v(-235, -75.83) * mm, "radius": 2.5 * mm});
            skCircle(sketch, "E194.8.7.0", {"center": v(-235, -105.83) * mm, "radius": 2.5 * mm});
            skCircle(sketch, "E194.8.8.0", {"center": v(-235, -135.83) * mm, "radius": 2.5 * mm});
            skLineSegment(sketch, "E194.direction1", {"start": v(-475, 104.17) * mm, "end": v(-445, 104.17) * mm, "construction": true});
            skLineSegment(sketch, "E194.direction2", {"start": v(-475, 104.17) * mm, "end": v(-475, 74.17) * mm, "construction": true});
            skSolve(sketch);
        }
        {
            var Q0;
            Q0 = qSketchRegion(id + "F2", true);
            extrude(context, id + "F3", {"entities" : qUnion([Q0]), "depth" : 5 * mm, "offsetDistance" : 25 * mm});
        }
    });
